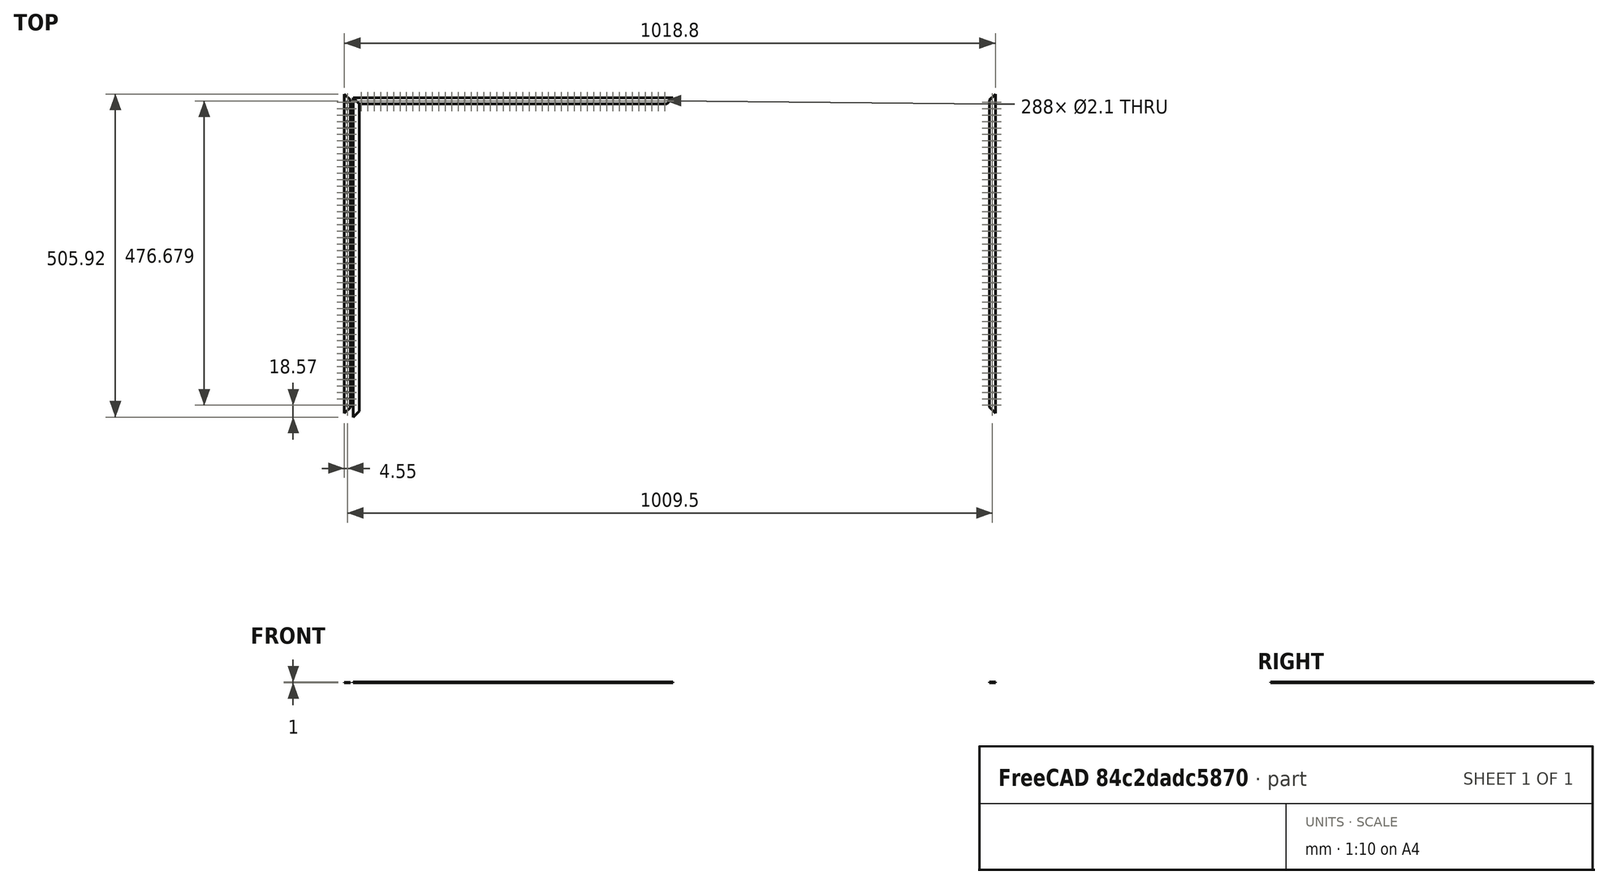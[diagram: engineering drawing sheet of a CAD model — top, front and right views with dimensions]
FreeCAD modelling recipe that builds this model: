
FCSTD DOCUMENT  (FreeCAD 0.21R)
Label: panneaux_solaires
License: All rights reserved
LicenseURL: http://en.wikipedia.org/wiki/All_rights_reserved
objects: Sketcher::SketchObject×112, PartDesign::Body×106, PartDesign::Pad×102, PartDesign::Pocket×8, App::DocumentObjectGroup×2, Part::Feature×1, Fem::ConstraintFixed×1, Fem::ConstraintForce×1, App::MaterialObjectPython×1, Fem::FemAnalysis×1
note: 439 computed .brp shape members not serialized (recipe doc carries the construction recipe); baked Part::Feature solids carry a one-line shape summary decoded from their .brp

FEATURE [Sketcher::SketchObject] Sketch001
  FullyConstrained = true
  MapMode = 5
  Placement = pos=(0,0,0) rot=(1,0,0;1.5708rad)
  sketch-geometry (8):
    g0: LineSegment StartX=0 StartY=0 StartZ=0 EndX=0 EndY=9.5 EndZ=0
    g1: LineSegment StartX=0 StartY=9.5 StartZ=0 EndX=1 EndY=9.5 EndZ=0
    g2: LineSegment StartX=1 StartY=9.5 StartZ=0 EndX=1 EndY=0 EndZ=0
    g3: LineSegment StartX=1 StartY=0 StartZ=0 EndX=0.8 EndY=0 EndZ=0
    g4: LineSegment StartX=0 StartY=0 StartZ=0 EndX=0.2 EndY=0 EndZ=0
    g5: LineSegment StartX=0.2 StartY=0 StartZ=0 EndX=0.2 EndY=9.3 EndZ=0
    g6: LineSegment StartX=0.2 StartY=9.3 StartZ=0 EndX=0.8 EndY=9.3 EndZ=0
    g7: LineSegment StartX=0.8 StartY=9.3 StartZ=0 EndX=0.8 EndY=0 EndZ=0
  constraints (23):
    c: Coincident(g0,g-1)
    c: PointOnObject(g0,g-2)
    c: Coincident(g1,g0)
    c: Horizontal(g1)
    c: Coincident(g2,g1)
    c: Vertical(g2)
    c: Coincident(g3,g2)
    c: Horizontal(g3)
    c: DistanceY(g2,g2) = 9.5
    c: DistanceY(g0,g0) = 9.5
    c: Coincident(g4,g0)
    c: PointOnObject(g4,g-1)
    c: Coincident(g5,g4)
    c: Vertical(g5)
    c: Coincident(g6,g5)
    c: Horizontal(g6)
    c: Coincident(g7,g6)
    c: Coincident(g7,g3)
    c: Vertical(g7)
    c: DistanceX(g1,g1) = 1
    c: DistanceX(g6,g6) = 0.6
    c: DistanceX(g4,g4) = 0.2
    c: DistanceY(g5,g5) = 9.3
FEATURE [PartDesign::Pad] Pad
  Direction = (0,-1,2e-16)
  Length = 500
  Length2 = 10
  Placement = pos=(0,0,0) rot=(1,0,0;1.5708rad)
  Profile = -> Sketch001
  ReferenceAxis = -> Sketch001 [N_Axis]
  Type = 0
FEATURE [Sketcher::SketchObject] Sketch
  FullyConstrained = false
  MapMode = 5
  Placement = pos=(0,0,0) rot=(0.57735,0.57735,0.57735;2.0944rad)
  sketch-geometry (3):
    g0: LineSegment StartX=0 StartY=-2.13969e-08 StartZ=0 EndX=0 EndY=9.5 EndZ=0
    g1: LineSegment StartX=-1.06984e-08 StartY=9.5 StartZ=0 EndX=-9.5 EndY=0 EndZ=0
    g2: LineSegment StartX=-9.5 StartY=0 StartZ=0 EndX=0 EndY=0 EndZ=0
  constraints (5):
    c: Vertical(g0)
    c: Horizontal(g2)
    c: DistanceX(g2,g2) = 9.5
    c: DistanceY(g0,g0) = 9.5
    c: Angle(g2,g1) = 0.785398
FEATURE [PartDesign::Pocket] Pocket
  BaseFeature = -> Pad
  Direction = (-1,-1e-16,1e-16)
  Length = 5
  Length2 = 5
  Placement = pos=(0,0,0) rot=(1,0,0;1.5708rad)
  Profile = -> Sketch
  ReferenceAxis = -> Sketch [N_Axis]
  Reversed = true
  Type = 1
FEATURE [Sketcher::SketchObject] Sketch002
  FullyConstrained = false
  MapMode = 5
  Placement = pos=(0,0,0) rot=(0.57735,0.57735,0.57735;2.0944rad)
  sketch-geometry (3):
    g0: LineSegment StartX=-500 StartY=0 StartZ=0 EndX=-490.5 EndY=0 EndZ=0
    g1: LineSegment StartX=-500 StartY=0 StartZ=0 EndX=-500 EndY=9.5 EndZ=0
    g2: LineSegment StartX=-490.5 StartY=0 StartZ=0 EndX=-500 EndY=9.5 EndZ=0
  constraints (7):
    c: Horizontal(g0)
    c: DistanceX(g0,g0) = 9.5
    c: Coincident(g1,g0)
    c: Vertical(g1)
    c: Coincident(g2,g0)
    c: Coincident(g2,g1)
    c: DistanceY(g1,g1) = 9.5
FEATURE [PartDesign::Pocket] Pocket001  label="cadre découoé"
  BaseFeature = -> Pocket
  Direction = (-1,-1e-16,1e-16)
  Length = 5
  Length2 = 5
  Placement = pos=(0,0,0) rot=(1,0,0;1.5708rad)
  Profile = -> Sketch002
  ReferenceAxis = -> Sketch002 [N_Axis]
  Reversed = true
  Type = 1
FEATURE [PartDesign::Body] Body  label="cadre gauche alu"
  Group = -> [Sketch001,Pad,Sketch,Pocket,Sketch002,Pocket001]
  Origin = -> Origin
  Placement = pos=(14.0463,-5.92123,0) rot=(0,0,0;1.5708rad)
  Tip = -> Pocket001
FEATURE [PartDesign::Body] Body002  label="percage pour rivet 7340a 2/3mm de structure"
  Origin = -> Origin002
FEATURE [Sketcher::SketchObject] Sketch007
  FullyConstrained = false
  MapMode = 5
  Placement = pos=(0,0.3,0) rot=(1,0,0;1.5708rad)
  sketch-geometry (8):
    g0: LineSegment StartX=0.6 StartY=9 StartZ=0 EndX=0.6 EndY=0 EndZ=0
    g1: LineSegment StartX=0.1 StartY=0 StartZ=0 EndX=0.1 EndY=8.9 EndZ=0
    g2: LineSegment StartX=0.1 StartY=8.9 StartZ=0 EndX=0.5 EndY=8.9 EndZ=0
    g3: LineSegment StartX=0.5 StartY=8.9 StartZ=0 EndX=0.5 EndY=0 EndZ=0
    g4: LineSegment StartX=0.6 StartY=0 StartZ=0 EndX=0.5 EndY=0 EndZ=0
    g5: LineSegment StartX=0 StartY=9 StartZ=0 EndX=0.6 EndY=9 EndZ=0
    g6: LineSegment StartX=0.1 StartY=0 StartZ=0 EndX=0 EndY=0 EndZ=0
    g7: LineSegment StartX=0 StartY=0 StartZ=0 EndX=0 EndY=9 EndZ=0
  constraints (21):
    c: Vertical(g0)
    c: DistanceY(g0,g0) = 9
    c: PointOnObject(g1,g-1)
    c: Vertical(g1)
    c: Coincident(g2,g1)
    c: Horizontal(g2)
    c: Coincident(g3,g2)
    c: Vertical(g3)
    c: DistanceX(g2,g2) = 0.4
    c: DistanceX(g-1,g1) = 0.1
    c: DistanceY(g1,g1) = 8.9
    c: Coincident(g4,g0)
    c: Coincident(g4,g3)
    c: Horizontal(g4)
    c: Coincident(g5,g0)
    c: Horizontal(g5)
    c: Coincident(g6,g1)
    c: Coincident(g6,g-1)
    c: Coincident(g7,g6)
    c: Coincident(g7,g5)
    c: Vertical(g7)
FEATURE [PartDesign::Pad] Pad001
  Direction = (0,-1,2e-16)
  Length = 500
  Length2 = 10
  Placement = pos=(0,0.3,0) rot=(1,0,0;1.5708rad)
  Profile = -> Sketch007
  ReferenceAxis = -> Sketch007 [N_Axis]
  Type = 0
FEATURE [Sketcher::SketchObject] Sketch008
  FullyConstrained = false
  MapMode = 5
  Placement = pos=(0,0,0) rot=(0.57735,0.57735,0.57735;2.0944rad)
  sketch-geometry (6):
    g0: LineSegment StartX=-499.7 StartY=9.2 StartZ=0 EndX=-499.7 EndY=-0.3 EndZ=0
    g1: LineSegment StartX=-499.7 StartY=-0.3 StartZ=0 EndX=-490.2 EndY=-0.3 EndZ=0
    g2: LineSegment StartX=-490.2 StartY=-0.3 StartZ=0 EndX=-499.7 EndY=9.2 EndZ=0
    g3: LineSegment StartX=0.3 StartY=-0.3 StartZ=0 EndX=-9.2 EndY=-0.3 EndZ=0
    g4: LineSegment StartX=0.3 StartY=-0.3 StartZ=0 EndX=0.3 EndY=9.2 EndZ=0
    g5: LineSegment StartX=0.3 StartY=9.2 StartZ=0 EndX=-9.2 EndY=-0.3 EndZ=0
  constraints (12):
    c: Vertical(g0)
    c: Horizontal(g1)
    c: Coincident(g2,g1)
    c: Coincident(g2,g0)
    c: DistanceY(g0,g0) = 9.5
    c: DistanceX(g1,g1) = 9.5
    c: Coincident(g4,g3)
    c: Vertical(g4)
    c: Coincident(g5,g3)
    c: Angle(g4,g3) = 1.5708
    c: DistanceY(g4,g4) = 9.5
    c: DistanceX(g3,g3) = 9.5
FEATURE [PartDesign::Pocket] Pocket002
  BaseFeature = -> Pad001
  Direction = (-1,-1e-16,1e-16)
  Length = 5
  Length2 = 5
  Placement = pos=(0,0.3,0) rot=(1,0,0;1.5708rad)
  Profile = -> Sketch008
  ReferenceAxis = -> Sketch008 [N_Axis]
  Reversed = true
  Type = 1
FEATURE [Sketcher::SketchObject] Sketch006
  FullyConstrained = true
  MapMode = 5
  sketch-geometry (48):
    g0: Circle CenterX=-4.75 CenterY=-487.35 CenterZ=0 NormalX=0 NormalY=0 NormalZ=1 AngleXU=0 Radius=1.05
    g1: Circle CenterX=-4.75 CenterY=-477.25 CenterZ=0 NormalX=0 NormalY=0 NormalZ=1 AngleXU=0 Radius=1.05
    g2: Circle CenterX=-4.75 CenterY=-457.05 CenterZ=0 NormalX=0 NormalY=0 NormalZ=1 AngleXU=0 Radius=1.05
    g3: Circle CenterX=-4.75 CenterY=-467.15 CenterZ=0 NormalX=0 NormalY=0 NormalZ=1 AngleXU=0 Radius=1.05
    g4: Circle CenterX=-4.75 CenterY=-416.65 CenterZ=0 NormalX=0 NormalY=0 NormalZ=1 AngleXU=0 Radius=1.05
    g5: Circle CenterX=-4.75 CenterY=-426.75 CenterZ=0 NormalX=0 NormalY=0 NormalZ=1 AngleXU=0 Radius=1.05
    g6: Circle CenterX=-4.75 CenterY=-436.85 CenterZ=0 NormalX=0 NormalY=0 NormalZ=1 AngleXU=0 Radius=1.05
    g7: Circle CenterX=-4.75 CenterY=-446.95 CenterZ=0 NormalX=0 NormalY=0 NormalZ=1 AngleXU=0 Radius=1.05
    g8: Circle CenterX=-4.75 CenterY=-335.85 CenterZ=0 NormalX=0 NormalY=0 NormalZ=1 AngleXU=0 Radius=1.05
    g9: Circle CenterX=-4.75 CenterY=-345.95 CenterZ=0 NormalX=0 NormalY=0 NormalZ=1 AngleXU=0 Radius=1.05
    g10: Circle CenterX=-4.75 CenterY=-356.05 CenterZ=0 NormalX=0 NormalY=0 NormalZ=1 AngleXU=0 Radius=1.05
    g11: Circle CenterX=-4.75 CenterY=-366.15 CenterZ=0 NormalX=0 NormalY=0 NormalZ=1 AngleXU=0 Radius=1.05
    g12: Circle CenterX=-4.75 CenterY=-376.25 CenterZ=0 NormalX=0 NormalY=0 NormalZ=1 AngleXU=0 Radius=1.05
    g13: Circle CenterX=-4.75 CenterY=-386.35 CenterZ=0 NormalX=0 NormalY=0 NormalZ=1 AngleXU=0 Radius=1.05
    g14: Circle CenterX=-4.75 CenterY=-396.45 CenterZ=0 NormalX=0 NormalY=0 NormalZ=1 AngleXU=0 Radius=1.05
    g15: Circle CenterX=-4.75 CenterY=-406.55 CenterZ=0 NormalX=0 NormalY=0 NormalZ=1 AngleXU=0 Radius=1.05
    g16: Circle CenterX=-4.75 CenterY=-174.25 CenterZ=0 NormalX=0 NormalY=0 NormalZ=1 AngleXU=0 Radius=1.05
    g17: Circle CenterX=-4.75 CenterY=-184.35 CenterZ=0 NormalX=0 NormalY=0 NormalZ=1 AngleXU=0 Radius=1.05
    g18: Circle CenterX=-4.75 CenterY=-194.45 CenterZ=0 NormalX=0 NormalY=0 NormalZ=1 AngleXU=0 Radius=1.05
    g19: Circle CenterX=-4.75 CenterY=-204.55 CenterZ=0 NormalX=0 NormalY=0 NormalZ=1 AngleXU=0 Radius=1.05
    g20: Circle CenterX=-4.75 CenterY=-214.65 CenterZ=0 NormalX=0 NormalY=0 NormalZ=1 AngleXU=0 Radius=1.05
    g21: Circle CenterX=-4.75 CenterY=-224.75 CenterZ=0 NormalX=0 NormalY=0 NormalZ=1 AngleXU=0 Radius=1.05
    g22: Circle CenterX=-4.75 CenterY=-234.85 CenterZ=0 NormalX=0 NormalY=0 NormalZ=1 AngleXU=0 Radius=1.05
    g23: Circle CenterX=-4.75 CenterY=-244.95 CenterZ=0 NormalX=0 NormalY=0 NormalZ=1 AngleXU=0 Radius=1.05
    g24: Circle CenterX=-4.75 CenterY=-255.05 CenterZ=0 NormalX=0 NormalY=0 NormalZ=1 AngleXU=0 Radius=1.05
    g25: Circle CenterX=-4.75 CenterY=-265.15 CenterZ=0 NormalX=0 NormalY=0 NormalZ=1 AngleXU=0 Radius=1.05
    g26: Circle CenterX=-4.75 CenterY=-275.25 CenterZ=0 NormalX=0 NormalY=0 NormalZ=1 AngleXU=0 Radius=1.05
    g27: Circle CenterX=-4.75 CenterY=-285.35 CenterZ=0 NormalX=0 NormalY=0 NormalZ=1 AngleXU=0 Radius=1.05
    g28: Circle CenterX=-4.75 CenterY=-295.45 CenterZ=0 NormalX=0 NormalY=0 NormalZ=1 AngleXU=0 Radius=1.05
    g29: Circle CenterX=-4.75 CenterY=-305.55 CenterZ=0 NormalX=0 NormalY=0 NormalZ=1 AngleXU=0 Radius=1.05
    g30: Circle CenterX=-4.75 CenterY=-315.65 CenterZ=0 NormalX=0 NormalY=0 NormalZ=1 AngleXU=0 Radius=1.05
    g31: Circle CenterX=-4.75 CenterY=-325.75 CenterZ=0 NormalX=0 NormalY=0 NormalZ=1 AngleXU=0 Radius=1.05
    g32: Circle CenterX=-4.75 CenterY=-63.15 CenterZ=0 NormalX=0 NormalY=0 NormalZ=1 AngleXU=0 Radius=1.05
    g33: Circle CenterX=-4.75 CenterY=-73.25 CenterZ=0 NormalX=0 NormalY=0 NormalZ=1 AngleXU=0 Radius=1.05
    g34: Circle CenterX=-4.75 CenterY=-83.35 CenterZ=0 NormalX=0 NormalY=0 NormalZ=1 AngleXU=0 Radius=1.05
    g35: Circle CenterX=-4.75 CenterY=-93.45 CenterZ=0 NormalX=0 NormalY=0 NormalZ=1 AngleXU=0 Radius=1.05
    g36: Circle CenterX=-4.75 CenterY=-103.55 CenterZ=0 NormalX=0 NormalY=0 NormalZ=1 AngleXU=0 Radius=1.05
    g37: Circle CenterX=-4.75 CenterY=-113.65 CenterZ=0 NormalX=0 NormalY=0 NormalZ=1 AngleXU=0 Radius=1.05
    g38: Circle CenterX=-4.75 CenterY=-123.75 CenterZ=0 NormalX=0 NormalY=0 NormalZ=1 AngleXU=0 Radius=1.05
    g39: Circle CenterX=-4.75 CenterY=-133.85 CenterZ=0 NormalX=0 NormalY=0 NormalZ=1 AngleXU=0 Radius=1.05
    g40: Circle CenterX=-4.75 CenterY=-143.95 CenterZ=0 NormalX=0 NormalY=0 NormalZ=1 AngleXU=0 Radius=1.05
    g41: Circle CenterX=-4.75 CenterY=-154.05 CenterZ=0 NormalX=0 NormalY=0 NormalZ=1 AngleXU=0 Radius=1.05
    g42: Circle CenterX=-4.75 CenterY=-164.15 CenterZ=0 NormalX=0 NormalY=0 NormalZ=1 AngleXU=0 Radius=1.05
    g43: Circle CenterX=-4.75 CenterY=-12.65 CenterZ=0 NormalX=0 NormalY=0 NormalZ=1 AngleXU=0 Radius=1.05
    g44: Circle CenterX=-4.75 CenterY=-22.75 CenterZ=0 NormalX=0 NormalY=0 NormalZ=1 AngleXU=0 Radius=1.05
    g45: Circle CenterX=-4.75 CenterY=-32.85 CenterZ=0 NormalX=0 NormalY=0 NormalZ=1 AngleXU=0 Radius=1.05
    g46: Circle CenterX=-4.75 CenterY=-42.95 CenterZ=0 NormalX=0 NormalY=0 NormalZ=1 AngleXU=0 Radius=1.05
    g47: Circle CenterX=-4.75 CenterY=-53.05 CenterZ=0 NormalX=0 NormalY=0 NormalZ=1 AngleXU=0 Radius=1.05
  constraints (144):
    c: Diameter(g0) = 2.1
    c: Equal(g0,g1) = 2.1
    c: DistanceY(g0,g1) = 10.1
    c: Equal(g0,g3) = 2.1
    c: Equal(g3,g2) = 2.1
    c: DistanceY(g3,g2) = 10.1
    c: Equal(g0,g7) = 2.1
    c: Equal(g7,g6) = 2.1
    c: DistanceY(g7,g6) = 10.1
    c: Equal(g7,g5) = 2.1
    c: Equal(g5,g4) = 2.1
    c: DistanceY(g5,g4) = 10.1
    c: Equal(g0,g15) = 2.1
    c: Equal(g15,g14) = 2.1
    c: DistanceY(g15,g14) = 10.1
    c: Equal(g15,g13) = 2.1
    c: Equal(g13,g12) = 2.1
    c: DistanceY(g13,g12) = 10.1
    c: Equal(g15,g11) = 2.1
    c: Equal(g11,g10) = 2.1
    c: DistanceY(g11,g10) = 10.1
    c: Equal(g11,g9) = 2.1
    c: Equal(g9,g8) = 2.1
    c: DistanceY(g9,g8) = 10.1
    c: Equal(g0,g31) = 2.1
    c: Equal(g31,g30) = 2.1
    c: DistanceY(g31,g30) = 10.1
    c: Equal(g31,g29) = 2.1
    c: Equal(g29,g28) = 2.1
    c: DistanceY(g29,g28) = 10.1
    c: Equal(g31,g27) = 2.1
    c: Equal(g27,g26) = 2.1
    c: DistanceY(g27,g26) = 10.1
    c: Equal(g27,g25) = 2.1
    c: Equal(g25,g24) = 2.1
    c: DistanceY(g25,g24) = 10.1
    c: Equal(g31,g23) = 2.1
    c: Equal(g23,g22) = 2.1
    c: DistanceY(g23,g22) = 10.1
    c: Equal(g23,g21) = 2.1
    c: Equal(g21,g20) = 2.1
    c: DistanceY(g21,g20) = 10.1
    c: Equal(g23,g19) = 2.1
    c: Equal(g19,g18) = 2.1
    c: DistanceY(g19,g18) = 10.1
    c: Equal(g19,g17) = 2.1
    c: Equal(g17,g16) = 2.1
    c: DistanceY(g17,g16) = 10.1
    c: Equal(g42,g41) = 2.1
    c: DistanceY(g42,g41) = 10.1
    c: Equal(g42,g40) = 2.1
    c: Equal(g40,g39) = 2.1
    c: DistanceY(g40,g39) = 10.1
    c: Equal(g38,g37) = 2.1
    c: DistanceY(g38,g37) = 10.1
    c: Equal(g38,g36) = 2.1
    c: Equal(g36,g35) = 2.1
    c: DistanceY(g36,g35) = 10.1
    c: Equal(g38,g34) = 2.1
    c: Equal(g34,g33) = 2.1
    c: DistanceY(g34,g33) = 10.1
    c: Equal(g34,g32) = 2.1
    c: Equal(g47,g46) = 2.1
    c: DistanceY(g47,g46) = 10.1
    c: Equal(g45,g44) = 2.1
    c: DistanceY(g45,g44) = 10.1
    c: Equal(g45,g43) = 2.1
    c: DistanceY(g1,g3) = 10.1
    c: DistanceY(g2,g7) = 10.1
    c: DistanceY(g6,g5) = 10.1
    c: DistanceY(g4,g15) = 10.1
    c: DistanceY(g14,g13) = 10.1
    c: DistanceY(g8,g31) = 10.1
    c: DistanceY(g30,g29) = 10.1
    c: DistanceY(g28,g27) = 10.1
    c: DistanceY(g26,g25) = 10.1
    c: DistanceY(g24,g23) = 10.1
    c: DistanceY(g22,g21) = 10.1
    c: DistanceY(g20,g19) = 10.1
    c: DistanceY(g18,g17) = 10.1
    c: DistanceY(g16,g42) = 10.1
    c: DistanceY(g39,g38) = 10.1
    c: DistanceY(g37,g36) = 10.1
    c: DistanceY(g35,g34) = 10.1
    c: DistanceY(g33,g32) = 10.1
    c: DistanceY(g46,g45) = 10.1
    c: DistanceY(g32,g47) = 10.1
    c: DistanceY(g44,g43) = 10.1
    c: DistanceY(g12,g11) = 10.1
    c: DistanceY(g10,g9) = 10.1
    c: DistanceY(g41,g40) = 10.1
    c: DistanceY(g43,g-1) = 12.65
    c: DistanceX(g43,g-1) = 4.75
    c: DistanceX(g44,g-1) = 4.75
    c: DistanceX(g45,g-1) = 4.75
    c: DistanceX(g47,g-1) = 4.75
    c: DistanceX(g32,g-1) = 4.75
    c: DistanceX(g34,g-1) = 4.75
    c: DistanceX(g35,g-1) = 4.75
    c: DistanceX(g0,g-1) = 4.75
    c: DistanceX(g1,g-1) = 4.75
    c: DistanceX(g3,g-1) = 4.75
    c: DistanceX(g2,g-1) = 4.75
    c: DistanceX(g7,g-1) = 4.75
    c: DistanceX(g6,g-1) = 4.75
    c: DistanceX(g5,g-1) = 4.75
    c: DistanceX(g4,g-1) = 4.75
    c: DistanceX(g15,g-1) = 4.75
    c: DistanceX(g14,g-1) = 4.75
    c: DistanceX(g13,g-1) = 4.75
    c: DistanceX(g12,g-1) = 4.75
    c: DistanceX(g11,g-1) = 4.75
    c: DistanceX(g10,g-1) = 4.75
    c: DistanceX(g9,g-1) = 4.75
    c: DistanceX(g8,g-1) = 4.75
    c: DistanceX(g31,g-1) = 4.75
    c: DistanceX(g30,g-1) = 4.75
    c: DistanceX(g29,g-1) = 4.75
    c: DistanceX(g28,g-1) = 4.75
    c: DistanceX(g27,g-1) = 4.75
    c: DistanceX(g26,g-1) = 4.75
    c: DistanceX(g25,g-1) = 4.75
    c: DistanceX(g24,g-1) = 4.75
    c: DistanceX(g23,g-1) = 4.75
    c: DistanceX(g22,g-1) = 4.75
    c: DistanceX(g21,g-1) = 4.75
    c: DistanceX(g20,g-1) = 4.75
    c: DistanceX(g19,g-1) = 4.75
    c: DistanceX(g18,g-1) = 4.75
    c: DistanceX(g17,g-1) = 4.75
    c: DistanceX(g16,g-1) = 4.75
    c: DistanceX(g42,g-1) = 4.75
    c: DistanceX(g41,g-1) = 4.75
    c: DistanceX(g40,g-1) = 4.75
    c: DistanceX(g39,g-1) = 4.75
    c: DistanceX(g38,g-1) = 4.75
    c: DistanceX(g37,g-1) = 4.75
    c: DistanceX(g36,g-1) = 4.75
    c: DistanceX(g33,g-1) = 4.75
    c: DistanceX(g46,g-1) = 4.75
    c: Diameter(g43) = 2.1
    c: Diameter(g46) = 2.1
    c: Diameter(g32) = 2.1
    c: Diameter(g39) = 2.1
FEATURE [PartDesign::Body] Body003  label="Corps"
  Group = -> [Sketch006]
  Origin = -> Origin003
FEATURE [Sketcher::SketchObject] Sketch010
  FullyConstrained = true
  MapMode = 5
  Placement = pos=(0,0.3,-0.3) rot=(0,1,0;1.5708rad)
  sketch-geometry (48):
    g0: Circle CenterX=-4.75 CenterY=-487.35 CenterZ=0 NormalX=0 NormalY=0 NormalZ=1 AngleXU=0 Radius=1.05
    g1: Circle CenterX=-4.75 CenterY=-477.25 CenterZ=0 NormalX=0 NormalY=0 NormalZ=1 AngleXU=0 Radius=1.05
    g2: Circle CenterX=-4.75 CenterY=-457.05 CenterZ=0 NormalX=0 NormalY=0 NormalZ=1 AngleXU=0 Radius=1.05
    g3: Circle CenterX=-4.75 CenterY=-467.15 CenterZ=0 NormalX=0 NormalY=0 NormalZ=1 AngleXU=0 Radius=1.05
    g4: Circle CenterX=-4.75 CenterY=-416.65 CenterZ=0 NormalX=0 NormalY=0 NormalZ=1 AngleXU=0 Radius=1.05
    g5: Circle CenterX=-4.75 CenterY=-426.75 CenterZ=0 NormalX=0 NormalY=0 NormalZ=1 AngleXU=0 Radius=1.05
    g6: Circle CenterX=-4.75 CenterY=-436.85 CenterZ=0 NormalX=0 NormalY=0 NormalZ=1 AngleXU=0 Radius=1.05
    g7: Circle CenterX=-4.75 CenterY=-446.95 CenterZ=0 NormalX=0 NormalY=0 NormalZ=1 AngleXU=0 Radius=1.05
    g8: Circle CenterX=-4.75 CenterY=-335.85 CenterZ=0 NormalX=0 NormalY=0 NormalZ=1 AngleXU=0 Radius=1.05
    g9: Circle CenterX=-4.75 CenterY=-345.95 CenterZ=0 NormalX=0 NormalY=0 NormalZ=1 AngleXU=0 Radius=1.05
    g10: Circle CenterX=-4.75 CenterY=-356.05 CenterZ=0 NormalX=0 NormalY=0 NormalZ=1 AngleXU=0 Radius=1.05
    g11: Circle CenterX=-4.75 CenterY=-366.15 CenterZ=0 NormalX=0 NormalY=0 NormalZ=1 AngleXU=0 Radius=1.05
    g12: Circle CenterX=-4.75 CenterY=-376.25 CenterZ=0 NormalX=0 NormalY=0 NormalZ=1 AngleXU=0 Radius=1.05
    g13: Circle CenterX=-4.75 CenterY=-386.35 CenterZ=0 NormalX=0 NormalY=0 NormalZ=1 AngleXU=0 Radius=1.05
    g14: Circle CenterX=-4.75 CenterY=-396.45 CenterZ=0 NormalX=0 NormalY=0 NormalZ=1 AngleXU=0 Radius=1.05
    g15: Circle CenterX=-4.75 CenterY=-406.55 CenterZ=0 NormalX=0 NormalY=0 NormalZ=1 AngleXU=0 Radius=1.05
    g16: Circle CenterX=-4.75 CenterY=-174.25 CenterZ=0 NormalX=0 NormalY=0 NormalZ=1 AngleXU=0 Radius=1.05
    g17: Circle CenterX=-4.75 CenterY=-184.35 CenterZ=0 NormalX=0 NormalY=0 NormalZ=1 AngleXU=0 Radius=1.05
    g18: Circle CenterX=-4.75 CenterY=-194.45 CenterZ=0 NormalX=0 NormalY=0 NormalZ=1 AngleXU=0 Radius=1.05
    g19: Circle CenterX=-4.75 CenterY=-204.55 CenterZ=0 NormalX=0 NormalY=0 NormalZ=1 AngleXU=0 Radius=1.05
    g20: Circle CenterX=-4.75 CenterY=-214.65 CenterZ=0 NormalX=0 NormalY=0 NormalZ=1 AngleXU=0 Radius=1.05
    g21: Circle CenterX=-4.75 CenterY=-224.75 CenterZ=0 NormalX=0 NormalY=0 NormalZ=1 AngleXU=0 Radius=1.05
    g22: Circle CenterX=-4.75 CenterY=-234.85 CenterZ=0 NormalX=0 NormalY=0 NormalZ=1 AngleXU=0 Radius=1.05
    g23: Circle CenterX=-4.75 CenterY=-244.95 CenterZ=0 NormalX=0 NormalY=0 NormalZ=1 AngleXU=0 Radius=1.05
    g24: Circle CenterX=-4.75 CenterY=-255.05 CenterZ=0 NormalX=0 NormalY=0 NormalZ=1 AngleXU=0 Radius=1.05
    g25: Circle CenterX=-4.75 CenterY=-265.15 CenterZ=0 NormalX=0 NormalY=0 NormalZ=1 AngleXU=0 Radius=1.05
    g26: Circle CenterX=-4.75 CenterY=-275.25 CenterZ=0 NormalX=0 NormalY=0 NormalZ=1 AngleXU=0 Radius=1.05
    g27: Circle CenterX=-4.75 CenterY=-285.35 CenterZ=0 NormalX=0 NormalY=0 NormalZ=1 AngleXU=0 Radius=1.05
    g28: Circle CenterX=-4.75 CenterY=-295.45 CenterZ=0 NormalX=0 NormalY=0 NormalZ=1 AngleXU=0 Radius=1.05
    g29: Circle CenterX=-4.75 CenterY=-305.55 CenterZ=0 NormalX=0 NormalY=0 NormalZ=1 AngleXU=0 Radius=1.05
    g30: Circle CenterX=-4.75 CenterY=-315.65 CenterZ=0 NormalX=0 NormalY=0 NormalZ=1 AngleXU=0 Radius=1.05
    g31: Circle CenterX=-4.75 CenterY=-325.75 CenterZ=0 NormalX=0 NormalY=0 NormalZ=1 AngleXU=0 Radius=1.05
    g32: Circle CenterX=-4.75 CenterY=-63.15 CenterZ=0 NormalX=0 NormalY=0 NormalZ=1 AngleXU=0 Radius=1.05
    g33: Circle CenterX=-4.75 CenterY=-73.25 CenterZ=0 NormalX=0 NormalY=0 NormalZ=1 AngleXU=0 Radius=1.05
    g34: Circle CenterX=-4.75 CenterY=-83.35 CenterZ=0 NormalX=0 NormalY=0 NormalZ=1 AngleXU=0 Radius=1.05
    g35: Circle CenterX=-4.75 CenterY=-93.45 CenterZ=0 NormalX=0 NormalY=0 NormalZ=1 AngleXU=0 Radius=1.05
    g36: Circle CenterX=-4.75 CenterY=-103.55 CenterZ=0 NormalX=0 NormalY=0 NormalZ=1 AngleXU=0 Radius=1.05
    g37: Circle CenterX=-4.75 CenterY=-113.65 CenterZ=0 NormalX=0 NormalY=0 NormalZ=1 AngleXU=0 Radius=1.05
    g38: Circle CenterX=-4.75 CenterY=-123.75 CenterZ=0 NormalX=0 NormalY=0 NormalZ=1 AngleXU=0 Radius=1.05
    g39: Circle CenterX=-4.75 CenterY=-133.85 CenterZ=0 NormalX=0 NormalY=0 NormalZ=1 AngleXU=0 Radius=1.05
    g40: Circle CenterX=-4.75 CenterY=-143.95 CenterZ=0 NormalX=0 NormalY=0 NormalZ=1 AngleXU=0 Radius=1.05
    g41: Circle CenterX=-4.75 CenterY=-154.05 CenterZ=0 NormalX=0 NormalY=0 NormalZ=1 AngleXU=0 Radius=1.05
    g42: Circle CenterX=-4.75 CenterY=-164.15 CenterZ=0 NormalX=0 NormalY=0 NormalZ=1 AngleXU=0 Radius=1.05
    g43: Circle CenterX=-4.75 CenterY=-12.65 CenterZ=0 NormalX=0 NormalY=0 NormalZ=1 AngleXU=0 Radius=1.05
    g44: Circle CenterX=-4.75 CenterY=-22.75 CenterZ=0 NormalX=0 NormalY=0 NormalZ=1 AngleXU=0 Radius=1.05
    g45: Circle CenterX=-4.75 CenterY=-32.85 CenterZ=0 NormalX=0 NormalY=0 NormalZ=1 AngleXU=0 Radius=1.05
    g46: Circle CenterX=-4.75 CenterY=-42.95 CenterZ=0 NormalX=0 NormalY=0 NormalZ=1 AngleXU=0 Radius=1.05
    g47: Circle CenterX=-4.75 CenterY=-53.05 CenterZ=0 NormalX=0 NormalY=0 NormalZ=1 AngleXU=0 Radius=1.05
  constraints (144):
    c: Diameter(g0) = 2.1
    c: Equal(g0,g1) = 2.1
    c: DistanceY(g0,g1) = 10.1
    c: Equal(g0,g3) = 2.1
    c: Equal(g3,g2) = 2.1
    c: DistanceY(g3,g2) = 10.1
    c: Equal(g0,g7) = 2.1
    c: Equal(g7,g6) = 2.1
    c: DistanceY(g7,g6) = 10.1
    c: Equal(g7,g5) = 2.1
    c: Equal(g5,g4) = 2.1
    c: DistanceY(g5,g4) = 10.1
    c: Equal(g0,g15) = 2.1
    c: Equal(g15,g14) = 2.1
    c: DistanceY(g15,g14) = 10.1
    c: Equal(g15,g13) = 2.1
    c: Equal(g13,g12) = 2.1
    c: DistanceY(g13,g12) = 10.1
    c: Equal(g15,g11) = 2.1
    c: Equal(g11,g10) = 2.1
    c: DistanceY(g11,g10) = 10.1
    c: Equal(g11,g9) = 2.1
    c: Equal(g9,g8) = 2.1
    c: DistanceY(g9,g8) = 10.1
    c: Equal(g0,g31) = 2.1
    c: Equal(g31,g30) = 2.1
    c: DistanceY(g31,g30) = 10.1
    c: Equal(g31,g29) = 2.1
    c: Equal(g29,g28) = 2.1
    c: DistanceY(g29,g28) = 10.1
    c: Equal(g31,g27) = 2.1
    c: Equal(g27,g26) = 2.1
    c: DistanceY(g27,g26) = 10.1
    c: Equal(g27,g25) = 2.1
    c: Equal(g25,g24) = 2.1
    c: DistanceY(g25,g24) = 10.1
    c: Equal(g31,g23) = 2.1
    c: Equal(g23,g22) = 2.1
    c: DistanceY(g23,g22) = 10.1
    c: Equal(g23,g21) = 2.1
    c: Equal(g21,g20) = 2.1
    c: DistanceY(g21,g20) = 10.1
    c: Equal(g23,g19) = 2.1
    c: Equal(g19,g18) = 2.1
    c: DistanceY(g19,g18) = 10.1
    c: Equal(g19,g17) = 2.1
    c: Equal(g17,g16) = 2.1
    c: DistanceY(g17,g16) = 10.1
    c: Equal(g42,g41) = 2.1
    c: DistanceY(g42,g41) = 10.1
    c: Equal(g42,g40) = 2.1
    c: Equal(g40,g39) = 2.1
    c: DistanceY(g40,g39) = 10.1
    c: Equal(g38,g37) = 2.1
    c: DistanceY(g38,g37) = 10.1
    c: Equal(g38,g36) = 2.1
    c: Equal(g36,g35) = 2.1
    c: DistanceY(g36,g35) = 10.1
    c: Equal(g38,g34) = 2.1
    c: Equal(g34,g33) = 2.1
    c: DistanceY(g34,g33) = 10.1
    c: Equal(g34,g32) = 2.1
    c: Equal(g47,g46) = 2.1
    c: DistanceY(g47,g46) = 10.1
    c: Equal(g45,g44) = 2.1
    c: DistanceY(g45,g44) = 10.1
    c: Equal(g45,g43) = 2.1
    c: DistanceY(g1,g3) = 10.1
    c: DistanceY(g2,g7) = 10.1
    c: DistanceY(g6,g5) = 10.1
    c: DistanceY(g4,g15) = 10.1
    c: DistanceY(g14,g13) = 10.1
    c: DistanceY(g8,g31) = 10.1
    c: DistanceY(g30,g29) = 10.1
    c: DistanceY(g28,g27) = 10.1
    c: DistanceY(g26,g25) = 10.1
    c: DistanceY(g24,g23) = 10.1
    c: DistanceY(g22,g21) = 10.1
    c: DistanceY(g20,g19) = 10.1
    c: DistanceY(g18,g17) = 10.1
    c: DistanceY(g16,g42) = 10.1
    c: DistanceY(g39,g38) = 10.1
    c: DistanceY(g37,g36) = 10.1
    c: DistanceY(g35,g34) = 10.1
    c: DistanceY(g33,g32) = 10.1
    c: DistanceY(g46,g45) = 10.1
    c: DistanceY(g32,g47) = 10.1
    c: DistanceY(g44,g43) = 10.1
    c: DistanceY(g12,g11) = 10.1
    c: DistanceY(g10,g9) = 10.1
    c: DistanceY(g41,g40) = 10.1
    c: DistanceY(g43,g-1) = 12.65
    c: DistanceX(g43,g-1) = 4.75
    c: DistanceX(g44,g-1) = 4.75
    c: DistanceX(g45,g-1) = 4.75
    c: DistanceX(g47,g-1) = 4.75
    c: DistanceX(g32,g-1) = 4.75
    c: DistanceX(g34,g-1) = 4.75
    c: DistanceX(g35,g-1) = 4.75
    c: DistanceX(g0,g-1) = 4.75
    c: DistanceX(g1,g-1) = 4.75
    c: DistanceX(g3,g-1) = 4.75
    c: DistanceX(g2,g-1) = 4.75
    c: DistanceX(g7,g-1) = 4.75
    c: DistanceX(g6,g-1) = 4.75
    c: DistanceX(g5,g-1) = 4.75
    c: DistanceX(g4,g-1) = 4.75
    c: DistanceX(g15,g-1) = 4.75
    c: DistanceX(g14,g-1) = 4.75
    c: DistanceX(g13,g-1) = 4.75
    c: DistanceX(g12,g-1) = 4.75
    c: DistanceX(g11,g-1) = 4.75
    c: DistanceX(g10,g-1) = 4.75
    c: DistanceX(g9,g-1) = 4.75
    c: DistanceX(g8,g-1) = 4.75
    c: DistanceX(g31,g-1) = 4.75
    c: DistanceX(g30,g-1) = 4.75
    c: DistanceX(g29,g-1) = 4.75
    c: DistanceX(g28,g-1) = 4.75
    c: DistanceX(g27,g-1) = 4.75
    c: DistanceX(g26,g-1) = 4.75
    c: DistanceX(g25,g-1) = 4.75
    c: DistanceX(g24,g-1) = 4.75
    c: DistanceX(g23,g-1) = 4.75
    c: DistanceX(g22,g-1) = 4.75
    c: DistanceX(g21,g-1) = 4.75
    c: DistanceX(g20,g-1) = 4.75
    c: DistanceX(g19,g-1) = 4.75
    c: DistanceX(g18,g-1) = 4.75
    c: DistanceX(g17,g-1) = 4.75
    c: DistanceX(g16,g-1) = 4.75
    c: DistanceX(g42,g-1) = 4.75
    c: DistanceX(g41,g-1) = 4.75
    c: DistanceX(g40,g-1) = 4.75
    c: DistanceX(g39,g-1) = 4.75
    c: DistanceX(g38,g-1) = 4.75
    c: DistanceX(g37,g-1) = 4.75
    c: DistanceX(g36,g-1) = 4.75
    c: DistanceX(g33,g-1) = 4.75
    c: DistanceX(g46,g-1) = 4.75
    c: Diameter(g43) = 2.1
    c: Diameter(g46) = 2.1
    c: Diameter(g32) = 2.1
    c: Diameter(g39) = 2.1
FEATURE [PartDesign::Pocket] Pocket003
  BaseFeature = -> Pocket002
  Direction = (-1,0,-2e-16)
  Length = 10
  Length2 = 5
  Placement = pos=(0,0.3,0) rot=(1,0,0;1.5708rad)
  Profile = -> Sketch010
  ReferenceAxis = -> Sketch010 [N_Axis]
  Refine = true
  Reversed = true
  Type = 1
FEATURE [PartDesign::Body] Body001  label="join caoutchou"
  Group = -> [Sketch007,Pad001,Sketch008,Pocket002,Sketch010,Pocket003]
  Origin = -> Origin001
  Placement = pos=(-0.3,-0.3,0.2) rot=(0,-1,0;1.5708rad)
  Tip = -> Pocket003
FEATURE [Sketcher::SketchObject] Sketch011
  FullyConstrained = true
  MapMode = 5
  sketch-geometry (1):
    g0: Circle CenterX=-4.75 CenterY=-22.75 CenterZ=0 NormalX=0 NormalY=0 NormalZ=1 AngleXU=0 Radius=1.05
  constraints (3):
    c: Diameter(g0) = 2.1
    c: Distance(g0,g-2) = 4.75
    c: Distance(g0,g-1) = 22.75
FEATURE [PartDesign::Pad] Pad003
  Direction = (0,0,1)
  Length = 0.6
  Length2 = 10
  Profile = -> Sketch011
  ReferenceAxis = -> Sketch011 [N_Axis]
  Refine = true
  Type = 0
FEATURE [PartDesign::Body] Body004  label="entretoises"
  Group = -> [Sketch011,Pad003]
  Origin = -> Origin004
  Tip = -> Pad003
FEATURE [Sketcher::SketchObject] Sketch012
  FullyConstrained = true
  MapMode = 5
  Placement = pos=(0,0,0.2) rot=(0,0,1;0rad)
  sketch-geometry (1):
    g0: Circle CenterX=-4.75 CenterY=-12.65 CenterZ=0 NormalX=0 NormalY=0 NormalZ=1 AngleXU=0 Radius=1.05
  constraints (3):
    c: Diameter(g0) = 2.1
    c: Distance(g0,g-2) = 4.75
    c: Distance(g0,g-1) = 12.65
FEATURE [PartDesign::Pad] Pad004
  Direction = (0,0,1)
  Length = 0.6
  Length2 = 10
  Placement = pos=(0,0,0.2) rot=(0,0,1;0rad)
  Profile = -> Sketch012
  ReferenceAxis = -> Sketch012 [N_Axis]
  Refine = true
  Type = 0
FEATURE [PartDesign::Body] Body005  label="entretoises001"
  Group = -> [Sketch012,Pad004]
  Origin = -> Origin005
  Tip = -> Pad004
FEATURE [Sketcher::SketchObject] Sketch013
  FullyConstrained = true
  MapMode = 5
  Placement = pos=(0,0,0.2) rot=(0,0,1;0rad)
  sketch-geometry (1):
    g0: Circle CenterX=-4.75 CenterY=-32.85 CenterZ=0 NormalX=0 NormalY=0 NormalZ=1 AngleXU=0 Radius=1.05
  constraints (3):
    c: Diameter(g0) = 2.1
    c: Distance(g0,g-2) = 4.75
    c: Distance(g0,g-1) = 32.85
FEATURE [PartDesign::Pad] Pad005
  Direction = (0,0,1)
  Length = 0.6
  Length2 = 10
  Placement = pos=(0,0,0.2) rot=(0,0,1;0rad)
  Profile = -> Sketch013
  ReferenceAxis = -> Sketch013 [N_Axis]
  Refine = true
  Type = 0
FEATURE [PartDesign::Body] Body006  label="entretoises002"
  Group = -> [Sketch013,Pad005]
  Origin = -> Origin006
  Tip = -> Pad005
FEATURE [Sketcher::SketchObject] Sketch014
  FullyConstrained = true
  MapMode = 5
  Placement = pos=(0,0,0.2) rot=(0,0,1;0rad)
  sketch-geometry (1):
    g0: Circle CenterX=-4.75 CenterY=-42.95 CenterZ=0 NormalX=0 NormalY=0 NormalZ=1 AngleXU=0 Radius=1.05
  constraints (3):
    c: Diameter(g0) = 2.1
    c: Distance(g0,g-2) = 4.75
    c: Distance(g0,g-1) = 42.95
FEATURE [PartDesign::Pad] Pad006
  Direction = (0,0,1)
  Length = 0.6
  Length2 = 10
  Placement = pos=(0,0,0.2) rot=(0,0,1;0rad)
  Profile = -> Sketch014
  ReferenceAxis = -> Sketch014 [N_Axis]
  Refine = true
  Type = 0
FEATURE [PartDesign::Body] Body007  label="entretoises003"
  Group = -> [Sketch014,Pad006]
  Origin = -> Origin007
  Tip = -> Pad006
FEATURE [Sketcher::SketchObject] Sketch015
  FullyConstrained = true
  MapMode = 5
  Placement = pos=(0,0,0.2) rot=(0,0,1;0rad)
  sketch-geometry (1):
    g0: Circle CenterX=-4.75 CenterY=-53.05 CenterZ=0 NormalX=0 NormalY=0 NormalZ=1 AngleXU=0 Radius=1.05
  constraints (3):
    c: Diameter(g0) = 2.1
    c: Distance(g0,g-2) = 4.75
    c: Distance(g0,g-1) = 53.05
FEATURE [PartDesign::Pad] Pad007
  Direction = (0,0,1)
  Length = 0.6
  Length2 = 10
  Placement = pos=(0,0,0.2) rot=(0,0,1;0rad)
  Profile = -> Sketch015
  ReferenceAxis = -> Sketch015 [N_Axis]
  Refine = true
  Type = 0
FEATURE [PartDesign::Body] Body008  label="entretoises004"
  Group = -> [Sketch015,Pad007]
  Origin = -> Origin008
  Tip = -> Pad007
FEATURE [Sketcher::SketchObject] Sketch016
  FullyConstrained = true
  MapMode = 5
  Placement = pos=(0,0,0.2) rot=(0,0,1;0rad)
  sketch-geometry (1):
    g0: Circle CenterX=-4.75 CenterY=-22.75 CenterZ=0 NormalX=0 NormalY=0 NormalZ=1 AngleXU=0 Radius=1.05
  constraints (3):
    c: Diameter(g0) = 2.1
    c: Distance(g0,g-2) = 4.75
    c: Distance(g0,g-1) = 22.75
FEATURE [PartDesign::Pad] Pad008
  Direction = (0,0,1)
  Length = 0.6
  Length2 = 10
  Placement = pos=(0,0,0.2) rot=(0,0,1;0rad)
  Profile = -> Sketch016
  ReferenceAxis = -> Sketch016 [N_Axis]
  Refine = true
  Type = 0
FEATURE [PartDesign::Body] Body009  label="entretoises005"
  Group = -> [Sketch016,Pad008]
  Origin = -> Origin009
  Tip = -> Pad008
FEATURE [Sketcher::SketchObject] Sketch017
  FullyConstrained = true
  MapMode = 5
  Placement = pos=(0,0,0.2) rot=(0,0,1;0rad)
  sketch-geometry (1):
    g0: Circle CenterX=-4.75 CenterY=-63.15 CenterZ=0 NormalX=0 NormalY=0 NormalZ=1 AngleXU=0 Radius=1.05
  constraints (3):
    c: Diameter(g0) = 2.1
    c: Distance(g0,g-2) = 4.75
    c: Distance(g0,g-1) = 63.15
FEATURE [Sketcher::SketchObject] Sketch018
  FullyConstrained = true
  MapMode = 5
  Placement = pos=(0,0,0.2) rot=(0,0,1;0rad)
  sketch-geometry (1):
    g0: Circle CenterX=-4.75 CenterY=-73.25 CenterZ=0 NormalX=0 NormalY=0 NormalZ=1 AngleXU=0 Radius=1.05
  constraints (3):
    c: Diameter(g0) = 2.1
    c: Distance(g0,g-2) = 4.75
    c: Distance(g0,g-1) = 73.25
FEATURE [PartDesign::Pad] Pad010
  Direction = (0,0,1)
  Length = 0.6
  Length2 = 10
  Placement = pos=(0,0,0.2) rot=(0,0,1;0rad)
  Profile = -> Sketch018
  ReferenceAxis = -> Sketch018 [N_Axis]
  Refine = true
  Type = 0
FEATURE [PartDesign::Body] Body011  label="entretoises007"
  Group = -> [Sketch018,Pad010]
  Origin = -> Origin011
  Tip = -> Pad010
FEATURE [Sketcher::SketchObject] Sketch019
  FullyConstrained = true
  MapMode = 5
  Placement = pos=(0,0,0.2) rot=(0,0,1;0rad)
  sketch-geometry (1):
    g0: Circle CenterX=-4.75 CenterY=-83.35 CenterZ=0 NormalX=0 NormalY=0 NormalZ=1 AngleXU=0 Radius=1.05
  constraints (3):
    c: Diameter(g0) = 2.1
    c: Distance(g0,g-2) = 4.75
    c: Distance(g0,g-1) = 83.35
FEATURE [PartDesign::Pad] Pad011
  Direction = (0,0,1)
  Length = 0.6
  Length2 = 10
  Placement = pos=(0,0,0.2) rot=(0,0,1;0rad)
  Profile = -> Sketch019
  ReferenceAxis = -> Sketch019 [N_Axis]
  Refine = true
  Type = 0
FEATURE [PartDesign::Body] Body012  label="entretoises008"
  Group = -> [Sketch019,Pad011]
  Origin = -> Origin012
  Tip = -> Pad011
FEATURE [Sketcher::SketchObject] Sketch020
  FullyConstrained = true
  MapMode = 5
  Placement = pos=(0,0,0.2) rot=(0,0,1;0rad)
  sketch-geometry (1):
    g0: Circle CenterX=-4.75 CenterY=-93.45 CenterZ=0 NormalX=0 NormalY=0 NormalZ=1 AngleXU=0 Radius=1.05
  constraints (3):
    c: Diameter(g0) = 2.1
    c: Distance(g0,g-2) = 4.75
    c: Distance(g0,g-1) = 93.45
FEATURE [PartDesign::Pad] Pad012
  Direction = (0,0,1)
  Length = 0.6
  Length2 = 10
  Placement = pos=(0,0,0.2) rot=(0,0,1;0rad)
  Profile = -> Sketch020
  ReferenceAxis = -> Sketch020 [N_Axis]
  Refine = true
  Type = 0
FEATURE [PartDesign::Body] Body013  label="entretoises009"
  Group = -> [Sketch020,Pad012]
  Origin = -> Origin013
  Tip = -> Pad012
FEATURE [Sketcher::SketchObject] Sketch021
  FullyConstrained = true
  MapMode = 5
  Placement = pos=(0,0,0.2) rot=(0,0,1;0rad)
  sketch-geometry (1):
    g0: Circle CenterX=-4.75 CenterY=-103.55 CenterZ=0 NormalX=0 NormalY=0 NormalZ=1 AngleXU=0 Radius=1.05
  constraints (3):
    c: Diameter(g0) = 2.1
    c: Distance(g0,g-2) = 4.75
    c: Distance(g0,g-1) = 103.55
FEATURE [PartDesign::Pad] Pad013
  Direction = (0,0,1)
  Length = 0.6
  Length2 = 10
  Placement = pos=(0,0,0.2) rot=(0,0,1;0rad)
  Profile = -> Sketch021
  ReferenceAxis = -> Sketch021 [N_Axis]
  Refine = true
  Type = 0
FEATURE [PartDesign::Body] Body014  label="entretoises010"
  Group = -> [Sketch021,Pad013]
  Origin = -> Origin014
  Tip = -> Pad013
FEATURE [Sketcher::SketchObject] Sketch022
  FullyConstrained = true
  MapMode = 5
  Placement = pos=(0,0,0.2) rot=(0,0,1;0rad)
  sketch-geometry (1):
    g0: Circle CenterX=-4.75 CenterY=-113.65 CenterZ=0 NormalX=0 NormalY=0 NormalZ=1 AngleXU=0 Radius=1.05
  constraints (3):
    c: Diameter(g0) = 2.1
    c: Distance(g0,g-2) = 4.75
    c: Distance(g0,g-1) = 113.65
FEATURE [PartDesign::Pad] Pad014
  Direction = (0,0,1)
  Length = 0.6
  Length2 = 10
  Placement = pos=(0,0,0.2) rot=(0,0,1;0rad)
  Profile = -> Sketch022
  ReferenceAxis = -> Sketch022 [N_Axis]
  Refine = true
  Type = 0
FEATURE [PartDesign::Body] Body015  label="entretoises011"
  Group = -> [Sketch022,Pad014]
  Origin = -> Origin015
  Tip = -> Pad014
FEATURE [Sketcher::SketchObject] Sketch023
  FullyConstrained = true
  MapMode = 5
  Placement = pos=(0,0,0.2) rot=(0,0,1;0rad)
  sketch-geometry (1):
    g0: Circle CenterX=-4.75 CenterY=-123.75 CenterZ=0 NormalX=0 NormalY=0 NormalZ=1 AngleXU=0 Radius=1.05
  constraints (3):
    c: Diameter(g0) = 2.1
    c: Distance(g0,g-2) = 4.75
    c: Distance(g0,g-1) = 123.75
FEATURE [PartDesign::Pad] Pad015
  Direction = (0,0,1)
  Length = 0.6
  Length2 = 10
  Placement = pos=(0,0,0.2) rot=(0,0,1;0rad)
  Profile = -> Sketch023
  ReferenceAxis = -> Sketch023 [N_Axis]
  Refine = true
  Type = 0
FEATURE [PartDesign::Body] Body016  label="entretoises012"
  Group = -> [Sketch023,Pad015]
  Origin = -> Origin016
  Tip = -> Pad015
FEATURE [Sketcher::SketchObject] Sketch024
  FullyConstrained = true
  MapMode = 5
  Placement = pos=(0,0,0.2) rot=(0,0,1;0rad)
  sketch-geometry (1):
    g0: Circle CenterX=-4.75 CenterY=-133.85 CenterZ=0 NormalX=0 NormalY=0 NormalZ=1 AngleXU=0 Radius=1.05
  constraints (3):
    c: Diameter(g0) = 2.1
    c: Distance(g0,g-2) = 4.75
    c: Distance(g0,g-1) = 133.85
FEATURE [PartDesign::Pad] Pad016
  Direction = (0,0,1)
  Length = 0.6
  Length2 = 10
  Placement = pos=(0,0,0.2) rot=(0,0,1;0rad)
  Profile = -> Sketch024
  ReferenceAxis = -> Sketch024 [N_Axis]
  Refine = true
  Type = 0
FEATURE [PartDesign::Body] Body017  label="entretoises013"
  Group = -> [Sketch024,Pad016]
  Origin = -> Origin017
  Tip = -> Pad016
FEATURE [Sketcher::SketchObject] Sketch025
  FullyConstrained = true
  MapMode = 5
  Placement = pos=(0,0,0.2) rot=(0,0,1;0rad)
  sketch-geometry (1):
    g0: Circle CenterX=-4.75 CenterY=-143.95 CenterZ=0 NormalX=0 NormalY=0 NormalZ=1 AngleXU=0 Radius=1.05
  constraints (3):
    c: Diameter(g0) = 2.1
    c: Distance(g0,g-2) = 4.75
    c: Distance(g0,g-1) = 143.95
FEATURE [PartDesign::Pad] Pad017
  Direction = (0,0,1)
  Length = 0.6
  Length2 = 10
  Placement = pos=(0,0,0.2) rot=(0,0,1;0rad)
  Profile = -> Sketch025
  ReferenceAxis = -> Sketch025 [N_Axis]
  Refine = true
  Type = 0
FEATURE [PartDesign::Body] Body018  label="entretoises014"
  Group = -> [Sketch025,Pad017]
  Origin = -> Origin018
  Tip = -> Pad017
FEATURE [Sketcher::SketchObject] Sketch026
  FullyConstrained = true
  MapMode = 5
  Placement = pos=(0,0,0.2) rot=(0,0,1;0rad)
  sketch-geometry (1):
    g0: Circle CenterX=-4.75 CenterY=-154.05 CenterZ=0 NormalX=0 NormalY=0 NormalZ=1 AngleXU=0 Radius=1.05
  constraints (3):
    c: Diameter(g0) = 2.1
    c: Distance(g0,g-2) = 4.75
    c: Distance(g0,g-1) = 154.05
FEATURE [PartDesign::Pad] Pad018
  Direction = (0,0,1)
  Length = 0.6
  Length2 = 10
  Placement = pos=(0,0,0.2) rot=(0,0,1;0rad)
  Profile = -> Sketch026
  ReferenceAxis = -> Sketch026 [N_Axis]
  Refine = true
  Type = 0
FEATURE [PartDesign::Body] Body019  label="entretoises015"
  Group = -> [Sketch026,Pad018]
  Origin = -> Origin019
  Tip = -> Pad018
FEATURE [Sketcher::SketchObject] Sketch027
  FullyConstrained = true
  MapMode = 5
  Placement = pos=(0,0,0.2) rot=(0,0,1;0rad)
  sketch-geometry (1):
    g0: Circle CenterX=-4.75 CenterY=-164.15 CenterZ=0 NormalX=0 NormalY=0 NormalZ=1 AngleXU=0 Radius=1.05
  constraints (3):
    c: Diameter(g0) = 2.1
    c: Distance(g0,g-2) = 4.75
    c: Distance(g0,g-1) = 164.15
FEATURE [PartDesign::Pad] Pad019
  Direction = (0,0,1)
  Length = 0.6
  Length2 = 10
  Placement = pos=(0,0,0.2) rot=(0,0,1;0rad)
  Profile = -> Sketch027
  ReferenceAxis = -> Sketch027 [N_Axis]
  Refine = true
  Type = 0
FEATURE [PartDesign::Body] Body020  label="entretoises016"
  Group = -> [Sketch027,Pad019]
  Origin = -> Origin020
  Tip = -> Pad019
FEATURE [Sketcher::SketchObject] Sketch028
  FullyConstrained = true
  MapMode = 5
  Placement = pos=(0,0,0.2) rot=(0,0,1;0rad)
  sketch-geometry (1):
    g0: Circle CenterX=-4.75 CenterY=-174.25 CenterZ=0 NormalX=0 NormalY=0 NormalZ=1 AngleXU=0 Radius=1.05
  constraints (3):
    c: Diameter(g0) = 2.1
    c: Distance(g0,g-2) = 4.75
    c: Distance(g0,g-1) = 174.25
FEATURE [PartDesign::Pad] Pad020
  Direction = (0,0,1)
  Length = 0.6
  Length2 = 10
  Placement = pos=(0,0,0.2) rot=(0,0,1;0rad)
  Profile = -> Sketch028
  ReferenceAxis = -> Sketch028 [N_Axis]
  Refine = true
  Type = 0
FEATURE [PartDesign::Body] Body021  label="entretoises017"
  Group = -> [Sketch028,Pad020]
  Origin = -> Origin021
  Tip = -> Pad020
FEATURE [Sketcher::SketchObject] Sketch029
  FullyConstrained = true
  MapMode = 5
  Placement = pos=(0,0,0.2) rot=(0,0,1;0rad)
  sketch-geometry (1):
    g0: Circle CenterX=-4.75 CenterY=-184.35 CenterZ=0 NormalX=0 NormalY=0 NormalZ=1 AngleXU=0 Radius=1.05
  constraints (3):
    c: Diameter(g0) = 2.1
    c: Distance(g0,g-2) = 4.75
    c: Distance(g0,g-1) = 184.35
FEATURE [PartDesign::Pad] Pad021
  Direction = (0,0,1)
  Length = 0.6
  Length2 = 10
  Placement = pos=(0,0,0.2) rot=(0,0,1;0rad)
  Profile = -> Sketch029
  ReferenceAxis = -> Sketch029 [N_Axis]
  Refine = true
  Type = 0
FEATURE [PartDesign::Body] Body022  label="entretoises018"
  Group = -> [Sketch029,Pad021]
  Origin = -> Origin022
  Tip = -> Pad021
FEATURE [Sketcher::SketchObject] Sketch030
  FullyConstrained = true
  MapMode = 5
  Placement = pos=(0,0,0.2) rot=(0,0,1;0rad)
  sketch-geometry (1):
    g0: Circle CenterX=-4.75 CenterY=-194.45 CenterZ=0 NormalX=0 NormalY=0 NormalZ=1 AngleXU=0 Radius=1.05
  constraints (3):
    c: Diameter(g0) = 2.1
    c: Distance(g0,g-2) = 4.75
    c: Distance(g0,g-1) = 194.45
FEATURE [PartDesign::Pad] Pad022
  Direction = (0,0,1)
  Length = 0.6
  Length2 = 10
  Placement = pos=(0,0,0.2) rot=(0,0,1;0rad)
  Profile = -> Sketch030
  ReferenceAxis = -> Sketch030 [N_Axis]
  Refine = true
  Type = 0
FEATURE [PartDesign::Body] Body023  label="entretoises019"
  Group = -> [Sketch030,Pad022]
  Origin = -> Origin023
  Tip = -> Pad022
FEATURE [Sketcher::SketchObject] Sketch031
  FullyConstrained = true
  MapMode = 5
  Placement = pos=(0,0,0.2) rot=(0,0,1;0rad)
  sketch-geometry (1):
    g0: Circle CenterX=-4.75 CenterY=-204.55 CenterZ=0 NormalX=0 NormalY=0 NormalZ=1 AngleXU=0 Radius=1.05
  constraints (3):
    c: Diameter(g0) = 2.1
    c: Distance(g0,g-2) = 4.75
    c: Distance(g0,g-1) = 204.55
FEATURE [PartDesign::Pad] Pad023
  Direction = (0,0,1)
  Length = 0.6
  Length2 = 10
  Placement = pos=(0,0,0.2) rot=(0,0,1;0rad)
  Profile = -> Sketch031
  ReferenceAxis = -> Sketch031 [N_Axis]
  Refine = true
  Type = 0
FEATURE [PartDesign::Body] Body024  label="entretoises020"
  Group = -> [Sketch031,Pad023]
  Origin = -> Origin024
  Tip = -> Pad023
FEATURE [Sketcher::SketchObject] Sketch032
  FullyConstrained = true
  MapMode = 5
  Placement = pos=(0,0,0.2) rot=(0,0,1;0rad)
  sketch-geometry (1):
    g0: Circle CenterX=-4.75 CenterY=-214.65 CenterZ=0 NormalX=0 NormalY=0 NormalZ=1 AngleXU=0 Radius=1.05
  constraints (3):
    c: Diameter(g0) = 2.1
    c: Distance(g0,g-2) = 4.75
    c: Distance(g0,g-1) = 214.65
FEATURE [PartDesign::Pad] Pad024
  Direction = (0,0,1)
  Length = 0.6
  Length2 = 10
  Placement = pos=(0,0,0.2) rot=(0,0,1;0rad)
  Profile = -> Sketch032
  ReferenceAxis = -> Sketch032 [N_Axis]
  Refine = true
  Type = 0
FEATURE [PartDesign::Body] Body025  label="entretoises021"
  Group = -> [Sketch032,Pad024]
  Origin = -> Origin025
  Tip = -> Pad024
FEATURE [Sketcher::SketchObject] Sketch033
  FullyConstrained = true
  MapMode = 5
  Placement = pos=(0,0,0.2) rot=(0,0,1;0rad)
  sketch-geometry (1):
    g0: Circle CenterX=-4.75 CenterY=-224.75 CenterZ=0 NormalX=0 NormalY=0 NormalZ=1 AngleXU=0 Radius=1.05
  constraints (3):
    c: Diameter(g0) = 2.1
    c: Distance(g0,g-2) = 4.75
    c: Distance(g0,g-1) = 224.75
FEATURE [PartDesign::Pad] Pad025
  Direction = (0,0,1)
  Length = 0.6
  Length2 = 10
  Placement = pos=(0,0,0.2) rot=(0,0,1;0rad)
  Profile = -> Sketch033
  ReferenceAxis = -> Sketch033 [N_Axis]
  Refine = true
  Type = 0
FEATURE [PartDesign::Body] Body026  label="entretoises022"
  Group = -> [Sketch033,Pad025]
  Origin = -> Origin026
  Tip = -> Pad025
FEATURE [Sketcher::SketchObject] Sketch034
  FullyConstrained = true
  MapMode = 5
  Placement = pos=(0,0,0.2) rot=(0,0,1;0rad)
  sketch-geometry (1):
    g0: Circle CenterX=-4.75 CenterY=-234.85 CenterZ=0 NormalX=0 NormalY=0 NormalZ=1 AngleXU=0 Radius=1.05
  constraints (3):
    c: Diameter(g0) = 2.1
    c: Distance(g0,g-2) = 4.75
    c: Distance(g0,g-1) = 234.85
FEATURE [PartDesign::Pad] Pad026
  Direction = (0,0,1)
  Length = 0.6
  Length2 = 10
  Placement = pos=(0,0,0.2) rot=(0,0,1;0rad)
  Profile = -> Sketch034
  ReferenceAxis = -> Sketch034 [N_Axis]
  Refine = true
  Type = 0
FEATURE [PartDesign::Body] Body027  label="entretoises023"
  Group = -> [Sketch034,Pad026]
  Origin = -> Origin027
  Tip = -> Pad026
FEATURE [Sketcher::SketchObject] Sketch035
  FullyConstrained = true
  MapMode = 5
  Placement = pos=(0,0,0.2) rot=(0,0,1;0rad)
  sketch-geometry (1):
    g0: Circle CenterX=-4.75 CenterY=-244.95 CenterZ=0 NormalX=0 NormalY=0 NormalZ=1 AngleXU=0 Radius=1.05
  constraints (3):
    c: Diameter(g0) = 2.1
    c: Distance(g0,g-2) = 4.75
    c: Distance(g0,g-1) = 244.95
FEATURE [PartDesign::Pad] Pad027
  Direction = (0,0,1)
  Length = 0.6
  Length2 = 10
  Placement = pos=(0,0,0.2) rot=(0,0,1;0rad)
  Profile = -> Sketch035
  ReferenceAxis = -> Sketch035 [N_Axis]
  Refine = true
  Type = 0
FEATURE [PartDesign::Body] Body028  label="entretoises024"
  Group = -> [Sketch035,Pad027]
  Origin = -> Origin028
  Tip = -> Pad027
FEATURE [Sketcher::SketchObject] Sketch036
  FullyConstrained = true
  MapMode = 5
  Placement = pos=(0,0,0.2) rot=(0,0,1;0rad)
  sketch-geometry (1):
    g0: Circle CenterX=-4.75 CenterY=-255.05 CenterZ=0 NormalX=0 NormalY=0 NormalZ=1 AngleXU=0 Radius=1.05
  constraints (3):
    c: Diameter(g0) = 2.1
    c: Distance(g0,g-2) = 4.75
    c: Distance(g0,g-1) = 255.05
FEATURE [PartDesign::Pad] Pad028
  Direction = (0,0,1)
  Length = 0.6
  Length2 = 10
  Placement = pos=(0,0,0.2) rot=(0,0,1;0rad)
  Profile = -> Sketch036
  ReferenceAxis = -> Sketch036 [N_Axis]
  Refine = true
  Type = 0
FEATURE [PartDesign::Body] Body029  label="entretoises025"
  Group = -> [Sketch036,Pad028]
  Origin = -> Origin029
  Tip = -> Pad028
FEATURE [Sketcher::SketchObject] Sketch037
  FullyConstrained = true
  MapMode = 5
  Placement = pos=(0,0,0.2) rot=(0,0,1;0rad)
  sketch-geometry (1):
    g0: Circle CenterX=-4.75 CenterY=-265.15 CenterZ=0 NormalX=0 NormalY=0 NormalZ=1 AngleXU=0 Radius=1.05
  constraints (3):
    c: Diameter(g0) = 2.1
    c: Distance(g0,g-2) = 4.75
    c: Distance(g0,g-1) = 265.15
FEATURE [PartDesign::Pad] Pad029
  Direction = (0,0,1)
  Length = 0.6
  Length2 = 10
  Placement = pos=(0,0,0.2) rot=(0,0,1;0rad)
  Profile = -> Sketch037
  ReferenceAxis = -> Sketch037 [N_Axis]
  Refine = true
  Type = 0
FEATURE [PartDesign::Body] Body030  label="entretoises026"
  Group = -> [Sketch037,Pad029]
  Origin = -> Origin030
  Tip = -> Pad029
FEATURE [Sketcher::SketchObject] Sketch038
  FullyConstrained = true
  MapMode = 5
  Placement = pos=(0,0,0.2) rot=(0,0,1;0rad)
  sketch-geometry (1):
    g0: Circle CenterX=-4.75 CenterY=-275.25 CenterZ=0 NormalX=0 NormalY=0 NormalZ=1 AngleXU=0 Radius=1.05
  constraints (3):
    c: Diameter(g0) = 2.1
    c: Distance(g0,g-2) = 4.75
    c: Distance(g0,g-1) = 275.25
FEATURE [PartDesign::Pad] Pad030
  Direction = (0,0,1)
  Length = 0.6
  Length2 = 10
  Placement = pos=(0,0,0.2) rot=(0,0,1;0rad)
  Profile = -> Sketch038
  ReferenceAxis = -> Sketch038 [N_Axis]
  Refine = true
  Type = 0
FEATURE [PartDesign::Body] Body031  label="entretoises027"
  Group = -> [Sketch038,Pad030]
  Origin = -> Origin031
  Tip = -> Pad030
FEATURE [Sketcher::SketchObject] Sketch039
  FullyConstrained = true
  MapMode = 5
  Placement = pos=(0,0,0.2) rot=(0,0,1;0rad)
  sketch-geometry (1):
    g0: Circle CenterX=-4.75 CenterY=-285.35 CenterZ=0 NormalX=0 NormalY=0 NormalZ=1 AngleXU=0 Radius=1.05
  constraints (3):
    c: Diameter(g0) = 2.1
    c: Distance(g0,g-2) = 4.75
    c: Distance(g0,g-1) = 285.35
FEATURE [PartDesign::Pad] Pad031
  Direction = (0,0,1)
  Length = 0.6
  Length2 = 10
  Placement = pos=(0,0,0.2) rot=(0,0,1;0rad)
  Profile = -> Sketch039
  ReferenceAxis = -> Sketch039 [N_Axis]
  Refine = true
  Type = 0
FEATURE [PartDesign::Body] Body032  label="entretoises028"
  Group = -> [Sketch039,Pad031]
  Origin = -> Origin032
  Tip = -> Pad031
FEATURE [Sketcher::SketchObject] Sketch040
  FullyConstrained = true
  MapMode = 5
  Placement = pos=(0,0,0.2) rot=(0,0,1;0rad)
  sketch-geometry (1):
    g0: Circle CenterX=-4.75 CenterY=-295.45 CenterZ=0 NormalX=0 NormalY=0 NormalZ=1 AngleXU=0 Radius=1.05
  constraints (3):
    c: Diameter(g0) = 2.1
    c: Distance(g0,g-2) = 4.75
    c: Distance(g0,g-1) = 295.45
FEATURE [PartDesign::Pad] Pad032
  Direction = (0,0,1)
  Length = 0.6
  Length2 = 10
  Placement = pos=(0,0,0.2) rot=(0,0,1;0rad)
  Profile = -> Sketch040
  ReferenceAxis = -> Sketch040 [N_Axis]
  Refine = true
  Type = 0
FEATURE [PartDesign::Body] Body033  label="entretoises029"
  Group = -> [Sketch040,Pad032]
  Origin = -> Origin033
  Tip = -> Pad032
FEATURE [Sketcher::SketchObject] Sketch041
  FullyConstrained = true
  MapMode = 5
  Placement = pos=(0,0,0.2) rot=(0,0,1;0rad)
  sketch-geometry (1):
    g0: Circle CenterX=-4.75 CenterY=-305.55 CenterZ=0 NormalX=0 NormalY=0 NormalZ=1 AngleXU=0 Radius=1.05
  constraints (3):
    c: Diameter(g0) = 2.1
    c: Distance(g0,g-2) = 4.75
    c: Distance(g0,g-1) = 305.55
FEATURE [PartDesign::Pad] Pad033
  Direction = (0,0,1)
  Length = 0.6
  Length2 = 10
  Placement = pos=(0,0,0.2) rot=(0,0,1;0rad)
  Profile = -> Sketch041
  ReferenceAxis = -> Sketch041 [N_Axis]
  Refine = true
  Type = 0
FEATURE [PartDesign::Body] Body034  label="entretoises030"
  Group = -> [Sketch041,Pad033]
  Origin = -> Origin034
  Tip = -> Pad033
FEATURE [Sketcher::SketchObject] Sketch042
  FullyConstrained = true
  MapMode = 5
  Placement = pos=(0,0,0.2) rot=(0,0,1;0rad)
  sketch-geometry (1):
    g0: Circle CenterX=-4.75 CenterY=-315.65 CenterZ=0 NormalX=0 NormalY=0 NormalZ=1 AngleXU=0 Radius=1.05
  constraints (3):
    c: Diameter(g0) = 2.1
    c: Distance(g0,g-2) = 4.75
    c: Distance(g0,g-1) = 315.65
FEATURE [PartDesign::Pad] Pad034
  Direction = (0,0,1)
  Length = 0.6
  Length2 = 10
  Placement = pos=(0,0,0.2) rot=(0,0,1;0rad)
  Profile = -> Sketch042
  ReferenceAxis = -> Sketch042 [N_Axis]
  Refine = true
  Type = 0
FEATURE [PartDesign::Body] Body035  label="entretoises031"
  Group = -> [Sketch042,Pad034]
  Origin = -> Origin035
  Tip = -> Pad034
FEATURE [Sketcher::SketchObject] Sketch043
  FullyConstrained = true
  MapMode = 5
  Placement = pos=(0,0,0.2) rot=(0,0,1;0rad)
  sketch-geometry (1):
    g0: Circle CenterX=-4.75 CenterY=-325.75 CenterZ=0 NormalX=0 NormalY=0 NormalZ=1 AngleXU=0 Radius=1.05
  constraints (3):
    c: Diameter(g0) = 2.1
    c: Distance(g0,g-2) = 4.75
    c: Distance(g0,g-1) = 325.75
FEATURE [PartDesign::Pad] Pad035
  Direction = (0,0,1)
  Length = 0.6
  Length2 = 10
  Placement = pos=(0,0,0.2) rot=(0,0,1;0rad)
  Profile = -> Sketch043
  ReferenceAxis = -> Sketch043 [N_Axis]
  Refine = true
  Type = 0
FEATURE [PartDesign::Body] Body036  label="entretoises032"
  Group = -> [Sketch043,Pad035]
  Origin = -> Origin036
  Tip = -> Pad035
FEATURE [Sketcher::SketchObject] Sketch044
  FullyConstrained = true
  MapMode = 5
  Placement = pos=(0,0,0.2) rot=(0,0,1;0rad)
  sketch-geometry (1):
    g0: Circle CenterX=-4.75 CenterY=-335.85 CenterZ=0 NormalX=0 NormalY=0 NormalZ=1 AngleXU=0 Radius=1.05
  constraints (3):
    c: Diameter(g0) = 2.1
    c: Distance(g0,g-2) = 4.75
    c: Distance(g0,g-1) = 335.85
FEATURE [PartDesign::Pad] Pad036
  Direction = (0,0,1)
  Length = 0.6
  Length2 = 10
  Placement = pos=(0,0,0.2) rot=(0,0,1;0rad)
  Profile = -> Sketch044
  ReferenceAxis = -> Sketch044 [N_Axis]
  Refine = true
  Type = 0
FEATURE [PartDesign::Body] Body037  label="entretoises033"
  Group = -> [Sketch044,Pad036]
  Origin = -> Origin037
  Tip = -> Pad036
FEATURE [Sketcher::SketchObject] Sketch045
  FullyConstrained = true
  MapMode = 5
  Placement = pos=(0,0,0.2) rot=(0,0,1;0rad)
  sketch-geometry (1):
    g0: Circle CenterX=-4.75 CenterY=-345.95 CenterZ=0 NormalX=0 NormalY=0 NormalZ=1 AngleXU=0 Radius=1.05
  constraints (3):
    c: Diameter(g0) = 2.1
    c: Distance(g0,g-2) = 4.75
    c: Distance(g0,g-1) = 345.95
FEATURE [PartDesign::Pad] Pad037
  Direction = (0,0,1)
  Length = 0.6
  Length2 = 10
  Placement = pos=(0,0,0.2) rot=(0,0,1;0rad)
  Profile = -> Sketch045
  ReferenceAxis = -> Sketch045 [N_Axis]
  Refine = true
  Type = 0
FEATURE [PartDesign::Body] Body038  label="entretoises034"
  Group = -> [Sketch045,Pad037]
  Origin = -> Origin038
  Tip = -> Pad037
FEATURE [Sketcher::SketchObject] Sketch046
  FullyConstrained = true
  MapMode = 5
  Placement = pos=(0,0,0.2) rot=(0,0,1;0rad)
  sketch-geometry (1):
    g0: Circle CenterX=-4.75 CenterY=-356.05 CenterZ=0 NormalX=0 NormalY=0 NormalZ=1 AngleXU=0 Radius=1.05
  constraints (3):
    c: Diameter(g0) = 2.1
    c: Distance(g0,g-2) = 4.75
    c: Distance(g0,g-1) = 356.05
FEATURE [PartDesign::Pad] Pad038
  Direction = (0,0,1)
  Length = 0.6
  Length2 = 10
  Placement = pos=(0,0,0.2) rot=(0,0,1;0rad)
  Profile = -> Sketch046
  ReferenceAxis = -> Sketch046 [N_Axis]
  Refine = true
  Type = 0
FEATURE [PartDesign::Body] Body039  label="entretoises035"
  Group = -> [Sketch046,Pad038]
  Origin = -> Origin039
  Tip = -> Pad038
FEATURE [Sketcher::SketchObject] Sketch047
  FullyConstrained = true
  MapMode = 5
  Placement = pos=(0,0,0.2) rot=(0,0,1;0rad)
  sketch-geometry (1):
    g0: Circle CenterX=-4.75 CenterY=-366.15 CenterZ=0 NormalX=0 NormalY=0 NormalZ=1 AngleXU=0 Radius=1.05
  constraints (3):
    c: Diameter(g0) = 2.1
    c: Distance(g0,g-2) = 4.75
    c: Distance(g0,g-1) = 366.15
FEATURE [PartDesign::Pad] Pad039
  Direction = (0,0,1)
  Length = 0.6
  Length2 = 10
  Placement = pos=(0,0,0.2) rot=(0,0,1;0rad)
  Profile = -> Sketch047
  ReferenceAxis = -> Sketch047 [N_Axis]
  Refine = true
  Type = 0
FEATURE [PartDesign::Body] Body040  label="entretoises036"
  Group = -> [Sketch047,Pad039]
  Origin = -> Origin040
  Tip = -> Pad039
FEATURE [Sketcher::SketchObject] Sketch048
  FullyConstrained = true
  MapMode = 5
  Placement = pos=(0,0,0.2) rot=(0,0,1;0rad)
  sketch-geometry (1):
    g0: Circle CenterX=-4.75 CenterY=-376.25 CenterZ=0 NormalX=0 NormalY=0 NormalZ=1 AngleXU=0 Radius=1.05
  constraints (3):
    c: Diameter(g0) = 2.1
    c: Distance(g0,g-2) = 4.75
    c: Distance(g0,g-1) = 376.25
FEATURE [PartDesign::Pad] Pad040
  Direction = (0,0,1)
  Length = 0.6
  Length2 = 10
  Placement = pos=(0,0,0.2) rot=(0,0,1;0rad)
  Profile = -> Sketch048
  ReferenceAxis = -> Sketch048 [N_Axis]
  Refine = true
  Type = 0
FEATURE [PartDesign::Body] Body041  label="entretoises037"
  Group = -> [Sketch048,Pad040]
  Origin = -> Origin041
  Tip = -> Pad040
FEATURE [Sketcher::SketchObject] Sketch049
  FullyConstrained = true
  MapMode = 5
  Placement = pos=(0,0,0.2) rot=(0,0,1;0rad)
  sketch-geometry (1):
    g0: Circle CenterX=-4.75 CenterY=-386.35 CenterZ=0 NormalX=0 NormalY=0 NormalZ=1 AngleXU=0 Radius=1.05
  constraints (3):
    c: Diameter(g0) = 2.1
    c: Distance(g0,g-2) = 4.75
    c: Distance(g0,g-1) = 386.35
FEATURE [PartDesign::Pad] Pad041
  Direction = (0,0,1)
  Length = 0.6
  Length2 = 10
  Placement = pos=(0,0,0.2) rot=(0,0,1;0rad)
  Profile = -> Sketch049
  ReferenceAxis = -> Sketch049 [N_Axis]
  Refine = true
  Type = 0
FEATURE [PartDesign::Body] Body042  label="entretoises038"
  Group = -> [Sketch049,Pad041]
  Origin = -> Origin042
  Tip = -> Pad041
FEATURE [Sketcher::SketchObject] Sketch050
  FullyConstrained = true
  MapMode = 5
  Placement = pos=(0,0,0.2) rot=(0,0,1;0rad)
  sketch-geometry (1):
    g0: Circle CenterX=-4.75 CenterY=-396.45 CenterZ=0 NormalX=0 NormalY=0 NormalZ=1 AngleXU=0 Radius=1.05
  constraints (3):
    c: Diameter(g0) = 2.1
    c: Distance(g0,g-2) = 4.75
    c: Distance(g0,g-1) = 396.45
FEATURE [PartDesign::Pad] Pad042
  Direction = (0,0,1)
  Length = 0.6
  Length2 = 10
  Placement = pos=(0,0,0.2) rot=(0,0,1;0rad)
  Profile = -> Sketch050
  ReferenceAxis = -> Sketch050 [N_Axis]
  Refine = true
  Type = 0
FEATURE [PartDesign::Body] Body043  label="entretoises039"
  Group = -> [Sketch050,Pad042]
  Origin = -> Origin043
  Tip = -> Pad042
FEATURE [Sketcher::SketchObject] Sketch051
  FullyConstrained = true
  MapMode = 5
  Placement = pos=(0,0,0.2) rot=(0,0,1;0rad)
  sketch-geometry (1):
    g0: Circle CenterX=-4.75 CenterY=-406.55 CenterZ=0 NormalX=0 NormalY=0 NormalZ=1 AngleXU=0 Radius=1.05
  constraints (3):
    c: Diameter(g0) = 2.1
    c: Distance(g0,g-2) = 4.75
    c: Distance(g0,g-1) = 406.55
FEATURE [PartDesign::Pad] Pad043
  Direction = (0,0,1)
  Length = 0.6
  Length2 = 10
  Placement = pos=(0,0,0.2) rot=(0,0,1;0rad)
  Profile = -> Sketch051
  ReferenceAxis = -> Sketch051 [N_Axis]
  Refine = true
  Type = 0
FEATURE [PartDesign::Body] Body044  label="entretoises040"
  Group = -> [Sketch051,Pad043]
  Origin = -> Origin044
  Tip = -> Pad043
FEATURE [Sketcher::SketchObject] Sketch052
  FullyConstrained = true
  MapMode = 5
  Placement = pos=(0,0,0.2) rot=(0,0,1;0rad)
  sketch-geometry (1):
    g0: Circle CenterX=-4.75 CenterY=-416.65 CenterZ=0 NormalX=0 NormalY=0 NormalZ=1 AngleXU=0 Radius=1.05
  constraints (3):
    c: Diameter(g0) = 2.1
    c: Distance(g0,g-2) = 4.75
    c: Distance(g0,g-1) = 416.65
FEATURE [PartDesign::Pad] Pad044
  Direction = (0,0,1)
  Length = 0.6
  Length2 = 10
  Placement = pos=(0,0,0.2) rot=(0,0,1;0rad)
  Profile = -> Sketch052
  ReferenceAxis = -> Sketch052 [N_Axis]
  Refine = true
  Type = 0
FEATURE [PartDesign::Body] Body045  label="entretoises041"
  Group = -> [Sketch052,Pad044]
  Origin = -> Origin045
  Tip = -> Pad044
FEATURE [Sketcher::SketchObject] Sketch053
  FullyConstrained = true
  MapMode = 5
  Placement = pos=(0,0,0.2) rot=(0,0,1;0rad)
  sketch-geometry (1):
    g0: Circle CenterX=-4.75 CenterY=-426.75 CenterZ=0 NormalX=0 NormalY=0 NormalZ=1 AngleXU=0 Radius=1.05
  constraints (3):
    c: Diameter(g0) = 2.1
    c: Distance(g0,g-2) = 4.75
    c: Distance(g0,g-1) = 426.75
FEATURE [PartDesign::Pad] Pad045
  Direction = (0,0,1)
  Length = 0.6
  Length2 = 10
  Placement = pos=(0,0,0.2) rot=(0,0,1;0rad)
  Profile = -> Sketch053
  ReferenceAxis = -> Sketch053 [N_Axis]
  Refine = true
  Type = 0
FEATURE [PartDesign::Body] Body046  label="entretoises042"
  Group = -> [Sketch053,Pad045]
  Origin = -> Origin046
  Tip = -> Pad045
FEATURE [Sketcher::SketchObject] Sketch054
  FullyConstrained = true
  MapMode = 5
  Placement = pos=(0,0,0.2) rot=(0,0,1;0rad)
  sketch-geometry (1):
    g0: Circle CenterX=-4.75 CenterY=-436.85 CenterZ=0 NormalX=0 NormalY=0 NormalZ=1 AngleXU=0 Radius=1.05
  constraints (3):
    c: Diameter(g0) = 2.1
    c: Distance(g0,g-2) = 4.75
    c: Distance(g0,g-1) = 436.85
FEATURE [PartDesign::Pad] Pad046
  Direction = (0,0,1)
  Length = 0.6
  Length2 = 10
  Placement = pos=(0,0,0.2) rot=(0,0,1;0rad)
  Profile = -> Sketch054
  ReferenceAxis = -> Sketch054 [N_Axis]
  Refine = true
  Type = 0
FEATURE [PartDesign::Body] Body047  label="entretoises043"
  Group = -> [Sketch054,Pad046]
  Origin = -> Origin047
  Tip = -> Pad046
FEATURE [Sketcher::SketchObject] Sketch055
  FullyConstrained = true
  MapMode = 5
  Placement = pos=(0,0,0.2) rot=(0,0,1;0rad)
  sketch-geometry (1):
    g0: Circle CenterX=-4.75 CenterY=-457.05 CenterZ=0 NormalX=0 NormalY=0 NormalZ=1 AngleXU=0 Radius=1.05
  constraints (3):
    c: Diameter(g0) = 2.1
    c: Distance(g0,g-2) = 4.75
    c: Distance(g0,g-1) = 457.05
FEATURE [PartDesign::Pad] Pad047
  Direction = (0,0,1)
  Length = 0.6
  Length2 = 10
  Placement = pos=(0,0,0.2) rot=(0,0,1;0rad)
  Profile = -> Sketch055
  ReferenceAxis = -> Sketch055 [N_Axis]
  Refine = true
  Type = 0
FEATURE [PartDesign::Body] Body048  label="entretoises044"
  Group = -> [Sketch055,Pad047]
  Origin = -> Origin048
  Tip = -> Pad047
FEATURE [PartDesign::Pad] Pad009
  Direction = (0,0,1)
  Length = 0.6
  Length2 = 10
  Placement = pos=(0,0,0.2) rot=(0,0,1;0rad)
  Profile = -> Sketch017
  ReferenceAxis = -> Sketch017 [N_Axis]
  Refine = true
  Type = 0
FEATURE [PartDesign::Body] Body010  label="entretoises006"
  Group = -> [Sketch017,Pad009]
  Origin = -> Origin010
  Tip = -> Pad009
FEATURE [Sketcher::SketchObject] Sketch056
  FullyConstrained = true
  MapMode = 5
  Placement = pos=(0,0,0.2) rot=(0,0,1;0rad)
  sketch-geometry (1):
    g0: Circle CenterX=-4.75 CenterY=-467.15 CenterZ=0 NormalX=0 NormalY=0 NormalZ=1 AngleXU=0 Radius=1.05
  constraints (3):
    c: Diameter(g0) = 2.1
    c: Distance(g0,g-2) = 4.75
    c: Distance(g0,g-1) = 467.15
FEATURE [PartDesign::Pad] Pad048
  Direction = (0,0,1)
  Length = 0.6
  Length2 = 10
  Placement = pos=(0,0,0.2) rot=(0,0,1;0rad)
  Profile = -> Sketch056
  ReferenceAxis = -> Sketch056 [N_Axis]
  Refine = true
  Type = 0
FEATURE [PartDesign::Body] Body049  label="entretoises045"
  Group = -> [Sketch056,Pad048]
  Origin = -> Origin049
  Tip = -> Pad048
FEATURE [Sketcher::SketchObject] Sketch057
  FullyConstrained = true
  MapMode = 5
  Placement = pos=(0,0,0.2) rot=(0,0,1;0rad)
  sketch-geometry (1):
    g0: Circle CenterX=-4.75 CenterY=-477.25 CenterZ=0 NormalX=0 NormalY=0 NormalZ=1 AngleXU=0 Radius=1.05
  constraints (3):
    c: Diameter(g0) = 2.1
    c: Distance(g0,g-2) = 4.75
    c: Distance(g0,g-1) = 477.25
FEATURE [PartDesign::Pad] Pad049
  Direction = (0,0,1)
  Length = 0.6
  Length2 = 10
  Placement = pos=(0,0,0.2) rot=(0,0,1;0rad)
  Profile = -> Sketch057
  ReferenceAxis = -> Sketch057 [N_Axis]
  Refine = true
  Type = 0
FEATURE [PartDesign::Body] Body050  label="entretoises046"
  Group = -> [Sketch057,Pad049]
  Origin = -> Origin050
  Tip = -> Pad049
FEATURE [Sketcher::SketchObject] Sketch058
  FullyConstrained = true
  MapMode = 5
  Placement = pos=(0,0,0.2) rot=(0,0,1;0rad)
  sketch-geometry (1):
    g0: Circle CenterX=-4.75 CenterY=-487.35 CenterZ=0 NormalX=0 NormalY=0 NormalZ=1 AngleXU=0 Radius=1.05
  constraints (3):
    c: Diameter(g0) = 2.1
    c: Distance(g0,g-2) = 4.75
    c: Distance(g0,g-1) = 487.35
FEATURE [PartDesign::Pad] Pad050
  Direction = (0,0,1)
  Length = 0.6
  Length2 = 10
  Placement = pos=(0,0,0.2) rot=(0,0,1;0rad)
  Profile = -> Sketch058
  ReferenceAxis = -> Sketch058 [N_Axis]
  Refine = true
  Type = 0
FEATURE [PartDesign::Body] Body051  label="entretoises047"
  Group = -> [Sketch058,Pad050]
  Origin = -> Origin051
  Tip = -> Pad050
FEATURE [Sketcher::SketchObject] Sketch059
  FullyConstrained = true
  MapMode = 5
  Placement = pos=(0,0,0.2) rot=(0,0,1;0rad)
  sketch-geometry (1):
    g0: Circle CenterX=-4.75 CenterY=-446.95 CenterZ=0 NormalX=0 NormalY=0 NormalZ=1 AngleXU=0 Radius=1.05
  constraints (3):
    c: Diameter(g0) = 2.1
    c: Distance(g0,g-2) = 4.75
    c: Distance(g0,g-1) = 446.95
FEATURE [PartDesign::Pad] Pad051
  Direction = (0,0,1)
  Length = 0.6
  Length2 = 10
  Placement = pos=(0,0,0.2) rot=(0,0,1;0rad)
  Profile = -> Sketch059
  ReferenceAxis = -> Sketch059 [N_Axis]
  Refine = true
  Type = 0
FEATURE [PartDesign::Body] Body052  label="entretoises048"
  Group = -> [Sketch059,Pad051]
  Origin = -> Origin052
  Tip = -> Pad051
FEATURE [App::DocumentObjectGroup] Group  label="cadre gauche"
  Group = -> [Body052,Body051,Body050,Body040,Body041,Body042,Body043,Body044,Body045,Body046,Body047,Body048,Body049,Body026,Body027,Body028,Body029,Body030,Body031,Body032,Body033,Body034,Body035,Body036,Body037,Body038,Body039,Body015,Body016,Body017,Body018,Body019,Body020,Body021,Body022,Body023,Body024,Body025,Body006,Body007,Body008,Body009,Body010,Body011,Body012,Body013,Body014,Body,Body001,Body002,+3 more]
FEATURE [Part::Feature] Group001  label="cadre droite"
  Placement = pos=(1000,-500,0) rot=(0,0,1;3.14159rad)
  shape: bbox 9.501 x 500 x 1.001 mm, 263 faces, 51 solids (baked)
FEATURE [PartDesign::Body] Body055  label="percage pour rivet 7340a 2/3mm de structure001"
  Origin = -> Origin055
  Placement = pos=(504.546,-15.4212,0) rot=(0,0,1;4.71239rad)
FEATURE [Sketcher::SketchObject] Sketch060
  FullyConstrained = false
  MapMode = 5
  Placement = pos=(0,0,0) rot=(0.57735,0.57735,0.57735;2.0944rad)
  sketch-geometry (3):
    g0: LineSegment StartX=0 StartY=-2.13969e-08 StartZ=0 EndX=0 EndY=9.5 EndZ=0
    g1: LineSegment StartX=-1.06984e-08 StartY=9.5 StartZ=0 EndX=-9.5 EndY=0 EndZ=0
    g2: LineSegment StartX=-9.5 StartY=0 StartZ=0 EndX=0 EndY=0 EndZ=0
  constraints (5):
    c: Vertical(g0)
    c: Horizontal(g2)
    c: DistanceX(g2,g2) = 9.5
    c: DistanceY(g0,g0) = 9.5
    c: Angle(g2,g1) = 0.785398
FEATURE [Sketcher::SketchObject] Sketch061
  FullyConstrained = true
  MapMode = 5
  Placement = pos=(0,0,0) rot=(1,0,0;1.5708rad)
  sketch-geometry (8):
    g0: LineSegment StartX=0 StartY=0 StartZ=0 EndX=0 EndY=9.5 EndZ=0
    g1: LineSegment StartX=0 StartY=9.5 StartZ=0 EndX=1 EndY=9.5 EndZ=0
    g2: LineSegment StartX=1 StartY=9.5 StartZ=0 EndX=1 EndY=0 EndZ=0
    g3: LineSegment StartX=1 StartY=0 StartZ=0 EndX=0.8 EndY=0 EndZ=0
    g4: LineSegment StartX=0 StartY=0 StartZ=0 EndX=0.2 EndY=0 EndZ=0
    g5: LineSegment StartX=0.2 StartY=0 StartZ=0 EndX=0.2 EndY=9.3 EndZ=0
    g6: LineSegment StartX=0.2 StartY=9.3 StartZ=0 EndX=0.8 EndY=9.3 EndZ=0
    g7: LineSegment StartX=0.8 StartY=9.3 StartZ=0 EndX=0.8 EndY=0 EndZ=0
  constraints (23):
    c: Coincident(g0,g-1)
    c: PointOnObject(g0,g-2)
    c: Coincident(g1,g0)
    c: Horizontal(g1)
    c: Coincident(g2,g1)
    c: Vertical(g2)
    c: Coincident(g3,g2)
    c: Horizontal(g3)
    c: DistanceY(g2,g2) = 9.5
    c: DistanceY(g0,g0) = 9.5
    c: Coincident(g4,g0)
    c: PointOnObject(g4,g-1)
    c: Coincident(g5,g4)
    c: Vertical(g5)
    c: Coincident(g6,g5)
    c: Horizontal(g6)
    c: Coincident(g7,g6)
    c: Coincident(g7,g3)
    c: Vertical(g7)
    c: DistanceX(g1,g1) = 1
    c: DistanceX(g6,g6) = 0.6
    c: DistanceX(g4,g4) = 0.2
    c: DistanceY(g5,g5) = 9.3
FEATURE [PartDesign::Pad] Pad052
  Direction = (0,-1,2e-16)
  Length = 500
  Length2 = 10
  Placement = pos=(0,0,0) rot=(1,0,0;1.5708rad)
  Profile = -> Sketch061
  ReferenceAxis = -> Sketch061 [N_Axis]
  Type = 0
FEATURE [PartDesign::Pocket] Pocket004
  BaseFeature = -> Pad052
  Direction = (-1,-1e-16,1e-16)
  Length = 5
  Length2 = 5
  Placement = pos=(0,0,0) rot=(1,0,0;1.5708rad)
  Profile = -> Sketch060
  ReferenceAxis = -> Sketch060 [N_Axis]
  Reversed = true
  Type = 1
FEATURE [Sketcher::SketchObject] Sketch062
  FullyConstrained = false
  MapMode = 5
  Placement = pos=(0,0,0) rot=(0.57735,0.57735,0.57735;2.0944rad)
  sketch-geometry (3):
    g0: LineSegment StartX=-500 StartY=0 StartZ=0 EndX=-490.5 EndY=0 EndZ=0
    g1: LineSegment StartX=-500 StartY=0 StartZ=0 EndX=-500 EndY=9.5 EndZ=0
    g2: LineSegment StartX=-490.5 StartY=0 StartZ=0 EndX=-500 EndY=9.5 EndZ=0
  constraints (7):
    c: Horizontal(g0)
    c: DistanceX(g0,g0) = 9.5
    c: Coincident(g1,g0)
    c: Vertical(g1)
    c: Coincident(g2,g0)
    c: Coincident(g2,g1)
    c: DistanceY(g1,g1) = 9.5
FEATURE [PartDesign::Pocket] Pocket005  label="cadre découoé001"
  BaseFeature = -> Pocket004
  Direction = (-1,-1e-16,1e-16)
  Length = 5
  Length2 = 5
  Placement = pos=(0,0,0) rot=(1,0,0;1.5708rad)
  Profile = -> Sketch062
  ReferenceAxis = -> Sketch062 [N_Axis]
  Reversed = true
  Type = 1
FEATURE [PartDesign::Body] Body053  label="cadre gauche alu001"
  Group = -> [Sketch061,Pad052,Sketch060,Pocket004,Sketch062,Pocket005]
  Origin = -> Origin053
  Placement = pos=(504.546,-15.4212,0) rot=(0.57735,0.57735,0.57735;4.18879rad)
  Tip = -> Pocket005
FEATURE [Sketcher::SketchObject] Sketch063
  FullyConstrained = true
  MapMode = 5
  sketch-geometry (48):
    g0: Circle CenterX=-4.75 CenterY=-487.35 CenterZ=0 NormalX=0 NormalY=0 NormalZ=1 AngleXU=0 Radius=1.05
    g1: Circle CenterX=-4.75 CenterY=-477.25 CenterZ=0 NormalX=0 NormalY=0 NormalZ=1 AngleXU=0 Radius=1.05
    g2: Circle CenterX=-4.75 CenterY=-457.05 CenterZ=0 NormalX=0 NormalY=0 NormalZ=1 AngleXU=0 Radius=1.05
    g3: Circle CenterX=-4.75 CenterY=-467.15 CenterZ=0 NormalX=0 NormalY=0 NormalZ=1 AngleXU=0 Radius=1.05
    g4: Circle CenterX=-4.75 CenterY=-416.65 CenterZ=0 NormalX=0 NormalY=0 NormalZ=1 AngleXU=0 Radius=1.05
    g5: Circle CenterX=-4.75 CenterY=-426.75 CenterZ=0 NormalX=0 NormalY=0 NormalZ=1 AngleXU=0 Radius=1.05
    g6: Circle CenterX=-4.75 CenterY=-436.85 CenterZ=0 NormalX=0 NormalY=0 NormalZ=1 AngleXU=0 Radius=1.05
    g7: Circle CenterX=-4.75 CenterY=-446.95 CenterZ=0 NormalX=0 NormalY=0 NormalZ=1 AngleXU=0 Radius=1.05
    g8: Circle CenterX=-4.75 CenterY=-335.85 CenterZ=0 NormalX=0 NormalY=0 NormalZ=1 AngleXU=0 Radius=1.05
    g9: Circle CenterX=-4.75 CenterY=-345.95 CenterZ=0 NormalX=0 NormalY=0 NormalZ=1 AngleXU=0 Radius=1.05
    g10: Circle CenterX=-4.75 CenterY=-356.05 CenterZ=0 NormalX=0 NormalY=0 NormalZ=1 AngleXU=0 Radius=1.05
    g11: Circle CenterX=-4.75 CenterY=-366.15 CenterZ=0 NormalX=0 NormalY=0 NormalZ=1 AngleXU=0 Radius=1.05
    g12: Circle CenterX=-4.75 CenterY=-376.25 CenterZ=0 NormalX=0 NormalY=0 NormalZ=1 AngleXU=0 Radius=1.05
    g13: Circle CenterX=-4.75 CenterY=-386.35 CenterZ=0 NormalX=0 NormalY=0 NormalZ=1 AngleXU=0 Radius=1.05
    g14: Circle CenterX=-4.75 CenterY=-396.45 CenterZ=0 NormalX=0 NormalY=0 NormalZ=1 AngleXU=0 Radius=1.05
    g15: Circle CenterX=-4.75 CenterY=-406.55 CenterZ=0 NormalX=0 NormalY=0 NormalZ=1 AngleXU=0 Radius=1.05
    g16: Circle CenterX=-4.75 CenterY=-174.25 CenterZ=0 NormalX=0 NormalY=0 NormalZ=1 AngleXU=0 Radius=1.05
    g17: Circle CenterX=-4.75 CenterY=-184.35 CenterZ=0 NormalX=0 NormalY=0 NormalZ=1 AngleXU=0 Radius=1.05
    g18: Circle CenterX=-4.75 CenterY=-194.45 CenterZ=0 NormalX=0 NormalY=0 NormalZ=1 AngleXU=0 Radius=1.05
    g19: Circle CenterX=-4.75 CenterY=-204.55 CenterZ=0 NormalX=0 NormalY=0 NormalZ=1 AngleXU=0 Radius=1.05
    g20: Circle CenterX=-4.75 CenterY=-214.65 CenterZ=0 NormalX=0 NormalY=0 NormalZ=1 AngleXU=0 Radius=1.05
    g21: Circle CenterX=-4.75 CenterY=-224.75 CenterZ=0 NormalX=0 NormalY=0 NormalZ=1 AngleXU=0 Radius=1.05
    g22: Circle CenterX=-4.75 CenterY=-234.85 CenterZ=0 NormalX=0 NormalY=0 NormalZ=1 AngleXU=0 Radius=1.05
    g23: Circle CenterX=-4.75 CenterY=-244.95 CenterZ=0 NormalX=0 NormalY=0 NormalZ=1 AngleXU=0 Radius=1.05
    g24: Circle CenterX=-4.75 CenterY=-255.05 CenterZ=0 NormalX=0 NormalY=0 NormalZ=1 AngleXU=0 Radius=1.05
    g25: Circle CenterX=-4.75 CenterY=-265.15 CenterZ=0 NormalX=0 NormalY=0 NormalZ=1 AngleXU=0 Radius=1.05
    g26: Circle CenterX=-4.75 CenterY=-275.25 CenterZ=0 NormalX=0 NormalY=0 NormalZ=1 AngleXU=0 Radius=1.05
    g27: Circle CenterX=-4.75 CenterY=-285.35 CenterZ=0 NormalX=0 NormalY=0 NormalZ=1 AngleXU=0 Radius=1.05
    g28: Circle CenterX=-4.75 CenterY=-295.45 CenterZ=0 NormalX=0 NormalY=0 NormalZ=1 AngleXU=0 Radius=1.05
    g29: Circle CenterX=-4.75 CenterY=-305.55 CenterZ=0 NormalX=0 NormalY=0 NormalZ=1 AngleXU=0 Radius=1.05
    g30: Circle CenterX=-4.75 CenterY=-315.65 CenterZ=0 NormalX=0 NormalY=0 NormalZ=1 AngleXU=0 Radius=1.05
    g31: Circle CenterX=-4.75 CenterY=-325.75 CenterZ=0 NormalX=0 NormalY=0 NormalZ=1 AngleXU=0 Radius=1.05
    g32: Circle CenterX=-4.75 CenterY=-63.15 CenterZ=0 NormalX=0 NormalY=0 NormalZ=1 AngleXU=0 Radius=1.05
    g33: Circle CenterX=-4.75 CenterY=-73.25 CenterZ=0 NormalX=0 NormalY=0 NormalZ=1 AngleXU=0 Radius=1.05
    g34: Circle CenterX=-4.75 CenterY=-83.35 CenterZ=0 NormalX=0 NormalY=0 NormalZ=1 AngleXU=0 Radius=1.05
    g35: Circle CenterX=-4.75 CenterY=-93.45 CenterZ=0 NormalX=0 NormalY=0 NormalZ=1 AngleXU=0 Radius=1.05
    g36: Circle CenterX=-4.75 CenterY=-103.55 CenterZ=0 NormalX=0 NormalY=0 NormalZ=1 AngleXU=0 Radius=1.05
    g37: Circle CenterX=-4.75 CenterY=-113.65 CenterZ=0 NormalX=0 NormalY=0 NormalZ=1 AngleXU=0 Radius=1.05
    g38: Circle CenterX=-4.75 CenterY=-123.75 CenterZ=0 NormalX=0 NormalY=0 NormalZ=1 AngleXU=0 Radius=1.05
    g39: Circle CenterX=-4.75 CenterY=-133.85 CenterZ=0 NormalX=0 NormalY=0 NormalZ=1 AngleXU=0 Radius=1.05
    g40: Circle CenterX=-4.75 CenterY=-143.95 CenterZ=0 NormalX=0 NormalY=0 NormalZ=1 AngleXU=0 Radius=1.05
    g41: Circle CenterX=-4.75 CenterY=-154.05 CenterZ=0 NormalX=0 NormalY=0 NormalZ=1 AngleXU=0 Radius=1.05
    g42: Circle CenterX=-4.75 CenterY=-164.15 CenterZ=0 NormalX=0 NormalY=0 NormalZ=1 AngleXU=0 Radius=1.05
    g43: Circle CenterX=-4.75 CenterY=-12.65 CenterZ=0 NormalX=0 NormalY=0 NormalZ=1 AngleXU=0 Radius=1.05
    g44: Circle CenterX=-4.75 CenterY=-22.75 CenterZ=0 NormalX=0 NormalY=0 NormalZ=1 AngleXU=0 Radius=1.05
    g45: Circle CenterX=-4.75 CenterY=-32.85 CenterZ=0 NormalX=0 NormalY=0 NormalZ=1 AngleXU=0 Radius=1.05
    g46: Circle CenterX=-4.75 CenterY=-42.95 CenterZ=0 NormalX=0 NormalY=0 NormalZ=1 AngleXU=0 Radius=1.05
    g47: Circle CenterX=-4.75 CenterY=-53.05 CenterZ=0 NormalX=0 NormalY=0 NormalZ=1 AngleXU=0 Radius=1.05
  constraints (144):
    c: Diameter(g0) = 2.1
    c: Equal(g0,g1) = 2.1
    c: DistanceY(g0,g1) = 10.1
    c: Equal(g0,g3) = 2.1
    c: Equal(g3,g2) = 2.1
    c: DistanceY(g3,g2) = 10.1
    c: Equal(g0,g7) = 2.1
    c: Equal(g7,g6) = 2.1
    c: DistanceY(g7,g6) = 10.1
    c: Equal(g7,g5) = 2.1
    c: Equal(g5,g4) = 2.1
    c: DistanceY(g5,g4) = 10.1
    c: Equal(g0,g15) = 2.1
    c: Equal(g15,g14) = 2.1
    c: DistanceY(g15,g14) = 10.1
    c: Equal(g15,g13) = 2.1
    c: Equal(g13,g12) = 2.1
    c: DistanceY(g13,g12) = 10.1
    c: Equal(g15,g11) = 2.1
    c: Equal(g11,g10) = 2.1
    c: DistanceY(g11,g10) = 10.1
    c: Equal(g11,g9) = 2.1
    c: Equal(g9,g8) = 2.1
    c: DistanceY(g9,g8) = 10.1
    c: Equal(g0,g31) = 2.1
    c: Equal(g31,g30) = 2.1
    c: DistanceY(g31,g30) = 10.1
    c: Equal(g31,g29) = 2.1
    c: Equal(g29,g28) = 2.1
    c: DistanceY(g29,g28) = 10.1
    c: Equal(g31,g27) = 2.1
    c: Equal(g27,g26) = 2.1
    c: DistanceY(g27,g26) = 10.1
    c: Equal(g27,g25) = 2.1
    c: Equal(g25,g24) = 2.1
    c: DistanceY(g25,g24) = 10.1
    c: Equal(g31,g23) = 2.1
    c: Equal(g23,g22) = 2.1
    c: DistanceY(g23,g22) = 10.1
    c: Equal(g23,g21) = 2.1
    c: Equal(g21,g20) = 2.1
    c: DistanceY(g21,g20) = 10.1
    c: Equal(g23,g19) = 2.1
    c: Equal(g19,g18) = 2.1
    c: DistanceY(g19,g18) = 10.1
    c: Equal(g19,g17) = 2.1
    c: Equal(g17,g16) = 2.1
    c: DistanceY(g17,g16) = 10.1
    c: Equal(g42,g41) = 2.1
    c: DistanceY(g42,g41) = 10.1
    c: Equal(g42,g40) = 2.1
    c: Equal(g40,g39) = 2.1
    c: DistanceY(g40,g39) = 10.1
    c: Equal(g38,g37) = 2.1
    c: DistanceY(g38,g37) = 10.1
    c: Equal(g38,g36) = 2.1
    c: Equal(g36,g35) = 2.1
    c: DistanceY(g36,g35) = 10.1
    c: Equal(g38,g34) = 2.1
    c: Equal(g34,g33) = 2.1
    c: DistanceY(g34,g33) = 10.1
    c: Equal(g34,g32) = 2.1
    c: Equal(g47,g46) = 2.1
    c: DistanceY(g47,g46) = 10.1
    c: Equal(g45,g44) = 2.1
    c: DistanceY(g45,g44) = 10.1
    c: Equal(g45,g43) = 2.1
    c: DistanceY(g1,g3) = 10.1
    c: DistanceY(g2,g7) = 10.1
    c: DistanceY(g6,g5) = 10.1
    c: DistanceY(g4,g15) = 10.1
    c: DistanceY(g14,g13) = 10.1
    c: DistanceY(g8,g31) = 10.1
    c: DistanceY(g30,g29) = 10.1
    c: DistanceY(g28,g27) = 10.1
    c: DistanceY(g26,g25) = 10.1
    c: DistanceY(g24,g23) = 10.1
    c: DistanceY(g22,g21) = 10.1
    c: DistanceY(g20,g19) = 10.1
    c: DistanceY(g18,g17) = 10.1
    c: DistanceY(g16,g42) = 10.1
    c: DistanceY(g39,g38) = 10.1
    c: DistanceY(g37,g36) = 10.1
    c: DistanceY(g35,g34) = 10.1
    c: DistanceY(g33,g32) = 10.1
    c: DistanceY(g46,g45) = 10.1
    c: DistanceY(g32,g47) = 10.1
    c: DistanceY(g44,g43) = 10.1
    c: DistanceY(g12,g11) = 10.1
    c: DistanceY(g10,g9) = 10.1
    c: DistanceY(g41,g40) = 10.1
    c: DistanceY(g43,g-1) = 12.65
    c: DistanceX(g43,g-1) = 4.75
    c: DistanceX(g44,g-1) = 4.75
    c: DistanceX(g45,g-1) = 4.75
    c: DistanceX(g47,g-1) = 4.75
    c: DistanceX(g32,g-1) = 4.75
    c: DistanceX(g34,g-1) = 4.75
    c: DistanceX(g35,g-1) = 4.75
    c: DistanceX(g0,g-1) = 4.75
    c: DistanceX(g1,g-1) = 4.75
    c: DistanceX(g3,g-1) = 4.75
    c: DistanceX(g2,g-1) = 4.75
    c: DistanceX(g7,g-1) = 4.75
    c: DistanceX(g6,g-1) = 4.75
    c: DistanceX(g5,g-1) = 4.75
    c: DistanceX(g4,g-1) = 4.75
    c: DistanceX(g15,g-1) = 4.75
    c: DistanceX(g14,g-1) = 4.75
    c: DistanceX(g13,g-1) = 4.75
    c: DistanceX(g12,g-1) = 4.75
    c: DistanceX(g11,g-1) = 4.75
    c: DistanceX(g10,g-1) = 4.75
    c: DistanceX(g9,g-1) = 4.75
    c: DistanceX(g8,g-1) = 4.75
    c: DistanceX(g31,g-1) = 4.75
    c: DistanceX(g30,g-1) = 4.75
    c: DistanceX(g29,g-1) = 4.75
    c: DistanceX(g28,g-1) = 4.75
    c: DistanceX(g27,g-1) = 4.75
    c: DistanceX(g26,g-1) = 4.75
    c: DistanceX(g25,g-1) = 4.75
    c: DistanceX(g24,g-1) = 4.75
    c: DistanceX(g23,g-1) = 4.75
    c: DistanceX(g22,g-1) = 4.75
    c: DistanceX(g21,g-1) = 4.75
    c: DistanceX(g20,g-1) = 4.75
    c: DistanceX(g19,g-1) = 4.75
    c: DistanceX(g18,g-1) = 4.75
    c: DistanceX(g17,g-1) = 4.75
    c: DistanceX(g16,g-1) = 4.75
    c: DistanceX(g42,g-1) = 4.75
    c: DistanceX(g41,g-1) = 4.75
    c: DistanceX(g40,g-1) = 4.75
    c: DistanceX(g39,g-1) = 4.75
    c: DistanceX(g38,g-1) = 4.75
    c: DistanceX(g37,g-1) = 4.75
    c: DistanceX(g36,g-1) = 4.75
    c: DistanceX(g33,g-1) = 4.75
    c: DistanceX(g46,g-1) = 4.75
    c: Diameter(g43) = 2.1
    c: Diameter(g46) = 2.1
    c: Diameter(g32) = 2.1
    c: Diameter(g39) = 2.1
FEATURE [PartDesign::Body] Body056  label="Corps001"
  Group = -> [Sketch063]
  Origin = -> Origin056
  Placement = pos=(504.546,-15.4212,0) rot=(0,0,1;4.71239rad)
FEATURE [Sketcher::SketchObject] Sketch064
  FullyConstrained = false
  MapMode = 5
  Placement = pos=(0,0.3,0) rot=(1,0,0;1.5708rad)
  sketch-geometry (8):
    g0: LineSegment StartX=0.6 StartY=9 StartZ=0 EndX=0.6 EndY=0 EndZ=0
    g1: LineSegment StartX=0.1 StartY=0 StartZ=0 EndX=0.1 EndY=8.9 EndZ=0
    g2: LineSegment StartX=0.1 StartY=8.9 StartZ=0 EndX=0.5 EndY=8.9 EndZ=0
    g3: LineSegment StartX=0.5 StartY=8.9 StartZ=0 EndX=0.5 EndY=0 EndZ=0
    g4: LineSegment StartX=0.6 StartY=0 StartZ=0 EndX=0.5 EndY=0 EndZ=0
    g5: LineSegment StartX=0 StartY=9 StartZ=0 EndX=0.6 EndY=9 EndZ=0
    g6: LineSegment StartX=0.1 StartY=0 StartZ=0 EndX=0 EndY=0 EndZ=0
    g7: LineSegment StartX=0 StartY=0 StartZ=0 EndX=0 EndY=9 EndZ=0
  constraints (21):
    c: Vertical(g0)
    c: DistanceY(g0,g0) = 9
    c: PointOnObject(g1,g-1)
    c: Vertical(g1)
    c: Coincident(g2,g1)
    c: Horizontal(g2)
    c: Coincident(g3,g2)
    c: Vertical(g3)
    c: DistanceX(g2,g2) = 0.4
    c: DistanceX(g-1,g1) = 0.1
    c: DistanceY(g1,g1) = 8.9
    c: Coincident(g4,g0)
    c: Coincident(g4,g3)
    c: Horizontal(g4)
    c: Coincident(g5,g0)
    c: Horizontal(g5)
    c: Coincident(g6,g1)
    c: Coincident(g6,g-1)
    c: Coincident(g7,g6)
    c: Coincident(g7,g5)
    c: Vertical(g7)
FEATURE [PartDesign::Pad] Pad053
  Direction = (0,-1,2e-16)
  Length = 500
  Length2 = 10
  Placement = pos=(0,0.3,0) rot=(1,0,0;1.5708rad)
  Profile = -> Sketch064
  ReferenceAxis = -> Sketch064 [N_Axis]
  Type = 0
FEATURE [Sketcher::SketchObject] Sketch065
  FullyConstrained = false
  MapMode = 5
  Placement = pos=(0,0,0) rot=(0.57735,0.57735,0.57735;2.0944rad)
  sketch-geometry (6):
    g0: LineSegment StartX=-499.7 StartY=9.2 StartZ=0 EndX=-499.7 EndY=-0.3 EndZ=0
    g1: LineSegment StartX=-499.7 StartY=-0.3 StartZ=0 EndX=-490.2 EndY=-0.3 EndZ=0
    g2: LineSegment StartX=-490.2 StartY=-0.3 StartZ=0 EndX=-499.7 EndY=9.2 EndZ=0
    g3: LineSegment StartX=0.3 StartY=-0.3 StartZ=0 EndX=-9.2 EndY=-0.3 EndZ=0
    g4: LineSegment StartX=0.3 StartY=-0.3 StartZ=0 EndX=0.3 EndY=9.2 EndZ=0
    g5: LineSegment StartX=0.3 StartY=9.2 StartZ=0 EndX=-9.2 EndY=-0.3 EndZ=0
  constraints (12):
    c: Vertical(g0)
    c: Horizontal(g1)
    c: Coincident(g2,g1)
    c: Coincident(g2,g0)
    c: DistanceY(g0,g0) = 9.5
    c: DistanceX(g1,g1) = 9.5
    c: Coincident(g4,g3)
    c: Vertical(g4)
    c: Coincident(g5,g3)
    c: Angle(g4,g3) = 1.5708
    c: DistanceY(g4,g4) = 9.5
    c: DistanceX(g3,g3) = 9.5
FEATURE [PartDesign::Pocket] Pocket006
  BaseFeature = -> Pad053
  Direction = (-1,-1e-16,1e-16)
  Length = 5
  Length2 = 5
  Placement = pos=(0,0.3,0) rot=(1,0,0;1.5708rad)
  Profile = -> Sketch065
  ReferenceAxis = -> Sketch065 [N_Axis]
  Reversed = true
  Type = 1
FEATURE [Sketcher::SketchObject] Sketch066
  FullyConstrained = true
  MapMode = 5
  Placement = pos=(0,0.3,-0.3) rot=(0,1,0;1.5708rad)
  sketch-geometry (48):
    g0: Circle CenterX=-4.75 CenterY=-487.35 CenterZ=0 NormalX=0 NormalY=0 NormalZ=1 AngleXU=0 Radius=1.05
    g1: Circle CenterX=-4.75 CenterY=-477.25 CenterZ=0 NormalX=0 NormalY=0 NormalZ=1 AngleXU=0 Radius=1.05
    g2: Circle CenterX=-4.75 CenterY=-457.05 CenterZ=0 NormalX=0 NormalY=0 NormalZ=1 AngleXU=0 Radius=1.05
    g3: Circle CenterX=-4.75 CenterY=-467.15 CenterZ=0 NormalX=0 NormalY=0 NormalZ=1 AngleXU=0 Radius=1.05
    g4: Circle CenterX=-4.75 CenterY=-416.65 CenterZ=0 NormalX=0 NormalY=0 NormalZ=1 AngleXU=0 Radius=1.05
    g5: Circle CenterX=-4.75 CenterY=-426.75 CenterZ=0 NormalX=0 NormalY=0 NormalZ=1 AngleXU=0 Radius=1.05
    g6: Circle CenterX=-4.75 CenterY=-436.85 CenterZ=0 NormalX=0 NormalY=0 NormalZ=1 AngleXU=0 Radius=1.05
    g7: Circle CenterX=-4.75 CenterY=-446.95 CenterZ=0 NormalX=0 NormalY=0 NormalZ=1 AngleXU=0 Radius=1.05
    g8: Circle CenterX=-4.75 CenterY=-335.85 CenterZ=0 NormalX=0 NormalY=0 NormalZ=1 AngleXU=0 Radius=1.05
    g9: Circle CenterX=-4.75 CenterY=-345.95 CenterZ=0 NormalX=0 NormalY=0 NormalZ=1 AngleXU=0 Radius=1.05
    g10: Circle CenterX=-4.75 CenterY=-356.05 CenterZ=0 NormalX=0 NormalY=0 NormalZ=1 AngleXU=0 Radius=1.05
    g11: Circle CenterX=-4.75 CenterY=-366.15 CenterZ=0 NormalX=0 NormalY=0 NormalZ=1 AngleXU=0 Radius=1.05
    g12: Circle CenterX=-4.75 CenterY=-376.25 CenterZ=0 NormalX=0 NormalY=0 NormalZ=1 AngleXU=0 Radius=1.05
    g13: Circle CenterX=-4.75 CenterY=-386.35 CenterZ=0 NormalX=0 NormalY=0 NormalZ=1 AngleXU=0 Radius=1.05
    g14: Circle CenterX=-4.75 CenterY=-396.45 CenterZ=0 NormalX=0 NormalY=0 NormalZ=1 AngleXU=0 Radius=1.05
    g15: Circle CenterX=-4.75 CenterY=-406.55 CenterZ=0 NormalX=0 NormalY=0 NormalZ=1 AngleXU=0 Radius=1.05
    g16: Circle CenterX=-4.75 CenterY=-174.25 CenterZ=0 NormalX=0 NormalY=0 NormalZ=1 AngleXU=0 Radius=1.05
    g17: Circle CenterX=-4.75 CenterY=-184.35 CenterZ=0 NormalX=0 NormalY=0 NormalZ=1 AngleXU=0 Radius=1.05
    g18: Circle CenterX=-4.75 CenterY=-194.45 CenterZ=0 NormalX=0 NormalY=0 NormalZ=1 AngleXU=0 Radius=1.05
    g19: Circle CenterX=-4.75 CenterY=-204.55 CenterZ=0 NormalX=0 NormalY=0 NormalZ=1 AngleXU=0 Radius=1.05
    g20: Circle CenterX=-4.75 CenterY=-214.65 CenterZ=0 NormalX=0 NormalY=0 NormalZ=1 AngleXU=0 Radius=1.05
    g21: Circle CenterX=-4.75 CenterY=-224.75 CenterZ=0 NormalX=0 NormalY=0 NormalZ=1 AngleXU=0 Radius=1.05
    g22: Circle CenterX=-4.75 CenterY=-234.85 CenterZ=0 NormalX=0 NormalY=0 NormalZ=1 AngleXU=0 Radius=1.05
    g23: Circle CenterX=-4.75 CenterY=-244.95 CenterZ=0 NormalX=0 NormalY=0 NormalZ=1 AngleXU=0 Radius=1.05
    g24: Circle CenterX=-4.75 CenterY=-255.05 CenterZ=0 NormalX=0 NormalY=0 NormalZ=1 AngleXU=0 Radius=1.05
    g25: Circle CenterX=-4.75 CenterY=-265.15 CenterZ=0 NormalX=0 NormalY=0 NormalZ=1 AngleXU=0 Radius=1.05
    g26: Circle CenterX=-4.75 CenterY=-275.25 CenterZ=0 NormalX=0 NormalY=0 NormalZ=1 AngleXU=0 Radius=1.05
    g27: Circle CenterX=-4.75 CenterY=-285.35 CenterZ=0 NormalX=0 NormalY=0 NormalZ=1 AngleXU=0 Radius=1.05
    g28: Circle CenterX=-4.75 CenterY=-295.45 CenterZ=0 NormalX=0 NormalY=0 NormalZ=1 AngleXU=0 Radius=1.05
    g29: Circle CenterX=-4.75 CenterY=-305.55 CenterZ=0 NormalX=0 NormalY=0 NormalZ=1 AngleXU=0 Radius=1.05
    g30: Circle CenterX=-4.75 CenterY=-315.65 CenterZ=0 NormalX=0 NormalY=0 NormalZ=1 AngleXU=0 Radius=1.05
    g31: Circle CenterX=-4.75 CenterY=-325.75 CenterZ=0 NormalX=0 NormalY=0 NormalZ=1 AngleXU=0 Radius=1.05
    g32: Circle CenterX=-4.75 CenterY=-63.15 CenterZ=0 NormalX=0 NormalY=0 NormalZ=1 AngleXU=0 Radius=1.05
    g33: Circle CenterX=-4.75 CenterY=-73.25 CenterZ=0 NormalX=0 NormalY=0 NormalZ=1 AngleXU=0 Radius=1.05
    g34: Circle CenterX=-4.75 CenterY=-83.35 CenterZ=0 NormalX=0 NormalY=0 NormalZ=1 AngleXU=0 Radius=1.05
    g35: Circle CenterX=-4.75 CenterY=-93.45 CenterZ=0 NormalX=0 NormalY=0 NormalZ=1 AngleXU=0 Radius=1.05
    g36: Circle CenterX=-4.75 CenterY=-103.55 CenterZ=0 NormalX=0 NormalY=0 NormalZ=1 AngleXU=0 Radius=1.05
    g37: Circle CenterX=-4.75 CenterY=-113.65 CenterZ=0 NormalX=0 NormalY=0 NormalZ=1 AngleXU=0 Radius=1.05
    g38: Circle CenterX=-4.75 CenterY=-123.75 CenterZ=0 NormalX=0 NormalY=0 NormalZ=1 AngleXU=0 Radius=1.05
    g39: Circle CenterX=-4.75 CenterY=-133.85 CenterZ=0 NormalX=0 NormalY=0 NormalZ=1 AngleXU=0 Radius=1.05
    g40: Circle CenterX=-4.75 CenterY=-143.95 CenterZ=0 NormalX=0 NormalY=0 NormalZ=1 AngleXU=0 Radius=1.05
    g41: Circle CenterX=-4.75 CenterY=-154.05 CenterZ=0 NormalX=0 NormalY=0 NormalZ=1 AngleXU=0 Radius=1.05
    g42: Circle CenterX=-4.75 CenterY=-164.15 CenterZ=0 NormalX=0 NormalY=0 NormalZ=1 AngleXU=0 Radius=1.05
    g43: Circle CenterX=-4.75 CenterY=-12.65 CenterZ=0 NormalX=0 NormalY=0 NormalZ=1 AngleXU=0 Radius=1.05
    g44: Circle CenterX=-4.75 CenterY=-22.75 CenterZ=0 NormalX=0 NormalY=0 NormalZ=1 AngleXU=0 Radius=1.05
    g45: Circle CenterX=-4.75 CenterY=-32.85 CenterZ=0 NormalX=0 NormalY=0 NormalZ=1 AngleXU=0 Radius=1.05
    g46: Circle CenterX=-4.75 CenterY=-42.95 CenterZ=0 NormalX=0 NormalY=0 NormalZ=1 AngleXU=0 Radius=1.05
    g47: Circle CenterX=-4.75 CenterY=-53.05 CenterZ=0 NormalX=0 NormalY=0 NormalZ=1 AngleXU=0 Radius=1.05
  constraints (144):
    c: Diameter(g0) = 2.1
    c: Equal(g0,g1) = 2.1
    c: DistanceY(g0,g1) = 10.1
    c: Equal(g0,g3) = 2.1
    c: Equal(g3,g2) = 2.1
    c: DistanceY(g3,g2) = 10.1
    c: Equal(g0,g7) = 2.1
    c: Equal(g7,g6) = 2.1
    c: DistanceY(g7,g6) = 10.1
    c: Equal(g7,g5) = 2.1
    c: Equal(g5,g4) = 2.1
    c: DistanceY(g5,g4) = 10.1
    c: Equal(g0,g15) = 2.1
    c: Equal(g15,g14) = 2.1
    c: DistanceY(g15,g14) = 10.1
    c: Equal(g15,g13) = 2.1
    c: Equal(g13,g12) = 2.1
    c: DistanceY(g13,g12) = 10.1
    c: Equal(g15,g11) = 2.1
    c: Equal(g11,g10) = 2.1
    c: DistanceY(g11,g10) = 10.1
    c: Equal(g11,g9) = 2.1
    c: Equal(g9,g8) = 2.1
    c: DistanceY(g9,g8) = 10.1
    c: Equal(g0,g31) = 2.1
    c: Equal(g31,g30) = 2.1
    c: DistanceY(g31,g30) = 10.1
    c: Equal(g31,g29) = 2.1
    c: Equal(g29,g28) = 2.1
    c: DistanceY(g29,g28) = 10.1
    c: Equal(g31,g27) = 2.1
    c: Equal(g27,g26) = 2.1
    c: DistanceY(g27,g26) = 10.1
    c: Equal(g27,g25) = 2.1
    c: Equal(g25,g24) = 2.1
    c: DistanceY(g25,g24) = 10.1
    c: Equal(g31,g23) = 2.1
    c: Equal(g23,g22) = 2.1
    c: DistanceY(g23,g22) = 10.1
    c: Equal(g23,g21) = 2.1
    c: Equal(g21,g20) = 2.1
    c: DistanceY(g21,g20) = 10.1
    c: Equal(g23,g19) = 2.1
    c: Equal(g19,g18) = 2.1
    c: DistanceY(g19,g18) = 10.1
    c: Equal(g19,g17) = 2.1
    c: Equal(g17,g16) = 2.1
    c: DistanceY(g17,g16) = 10.1
    c: Equal(g42,g41) = 2.1
    c: DistanceY(g42,g41) = 10.1
    c: Equal(g42,g40) = 2.1
    c: Equal(g40,g39) = 2.1
    c: DistanceY(g40,g39) = 10.1
    c: Equal(g38,g37) = 2.1
    c: DistanceY(g38,g37) = 10.1
    c: Equal(g38,g36) = 2.1
    c: Equal(g36,g35) = 2.1
    c: DistanceY(g36,g35) = 10.1
    c: Equal(g38,g34) = 2.1
    c: Equal(g34,g33) = 2.1
    c: DistanceY(g34,g33) = 10.1
    c: Equal(g34,g32) = 2.1
    c: Equal(g47,g46) = 2.1
    c: DistanceY(g47,g46) = 10.1
    c: Equal(g45,g44) = 2.1
    c: DistanceY(g45,g44) = 10.1
    c: Equal(g45,g43) = 2.1
    c: DistanceY(g1,g3) = 10.1
    c: DistanceY(g2,g7) = 10.1
    c: DistanceY(g6,g5) = 10.1
    c: DistanceY(g4,g15) = 10.1
    c: DistanceY(g14,g13) = 10.1
    c: DistanceY(g8,g31) = 10.1
    c: DistanceY(g30,g29) = 10.1
    c: DistanceY(g28,g27) = 10.1
    c: DistanceY(g26,g25) = 10.1
    c: DistanceY(g24,g23) = 10.1
    c: DistanceY(g22,g21) = 10.1
    c: DistanceY(g20,g19) = 10.1
    c: DistanceY(g18,g17) = 10.1
    c: DistanceY(g16,g42) = 10.1
    c: DistanceY(g39,g38) = 10.1
    c: DistanceY(g37,g36) = 10.1
    c: DistanceY(g35,g34) = 10.1
    c: DistanceY(g33,g32) = 10.1
    c: DistanceY(g46,g45) = 10.1
    c: DistanceY(g32,g47) = 10.1
    c: DistanceY(g44,g43) = 10.1
    c: DistanceY(g12,g11) = 10.1
    c: DistanceY(g10,g9) = 10.1
    c: DistanceY(g41,g40) = 10.1
    c: DistanceY(g43,g-1) = 12.65
    c: DistanceX(g43,g-1) = 4.75
    c: DistanceX(g44,g-1) = 4.75
    c: DistanceX(g45,g-1) = 4.75
    c: DistanceX(g47,g-1) = 4.75
    c: DistanceX(g32,g-1) = 4.75
    c: DistanceX(g34,g-1) = 4.75
    c: DistanceX(g35,g-1) = 4.75
    c: DistanceX(g0,g-1) = 4.75
    c: DistanceX(g1,g-1) = 4.75
    c: DistanceX(g3,g-1) = 4.75
    c: DistanceX(g2,g-1) = 4.75
    c: DistanceX(g7,g-1) = 4.75
    c: DistanceX(g6,g-1) = 4.75
    c: DistanceX(g5,g-1) = 4.75
    c: DistanceX(g4,g-1) = 4.75
    c: DistanceX(g15,g-1) = 4.75
    c: DistanceX(g14,g-1) = 4.75
    c: DistanceX(g13,g-1) = 4.75
    c: DistanceX(g12,g-1) = 4.75
    c: DistanceX(g11,g-1) = 4.75
    c: DistanceX(g10,g-1) = 4.75
    c: DistanceX(g9,g-1) = 4.75
    c: DistanceX(g8,g-1) = 4.75
    c: DistanceX(g31,g-1) = 4.75
    c: DistanceX(g30,g-1) = 4.75
    c: DistanceX(g29,g-1) = 4.75
    c: DistanceX(g28,g-1) = 4.75
    c: DistanceX(g27,g-1) = 4.75
    c: DistanceX(g26,g-1) = 4.75
    c: DistanceX(g25,g-1) = 4.75
    c: DistanceX(g24,g-1) = 4.75
    c: DistanceX(g23,g-1) = 4.75
    c: DistanceX(g22,g-1) = 4.75
    c: DistanceX(g21,g-1) = 4.75
    c: DistanceX(g20,g-1) = 4.75
    c: DistanceX(g19,g-1) = 4.75
    c: DistanceX(g18,g-1) = 4.75
    c: DistanceX(g17,g-1) = 4.75
    c: DistanceX(g16,g-1) = 4.75
    c: DistanceX(g42,g-1) = 4.75
    c: DistanceX(g41,g-1) = 4.75
    c: DistanceX(g40,g-1) = 4.75
    c: DistanceX(g39,g-1) = 4.75
    c: DistanceX(g38,g-1) = 4.75
    c: DistanceX(g37,g-1) = 4.75
    c: DistanceX(g36,g-1) = 4.75
    c: DistanceX(g33,g-1) = 4.75
    c: DistanceX(g46,g-1) = 4.75
    c: Diameter(g43) = 2.1
    c: Diameter(g46) = 2.1
    c: Diameter(g32) = 2.1
    c: Diameter(g39) = 2.1
FEATURE [PartDesign::Pocket] Pocket007
  BaseFeature = -> Pocket006
  Direction = (-1,0,-2e-16)
  Length = 10
  Length2 = 5
  Placement = pos=(0,0.3,0) rot=(1,0,0;1.5708rad)
  Profile = -> Sketch066
  ReferenceAxis = -> Sketch066 [N_Axis]
  Refine = true
  Reversed = true
  Type = 1
FEATURE [PartDesign::Body] Body054  label="join caoutchou001"
  Group = -> [Sketch064,Pad053,Sketch065,Pocket006,Sketch066,Pocket007]
  Origin = -> Origin054
  Placement = pos=(504.246,-15.1212,0.2) rot=(0.57735,0.57735,0.57735;4.18879rad)
  Tip = -> Pocket007
FEATURE [Sketcher::SketchObject] Sketch067
  FullyConstrained = true
  MapMode = 5
  sketch-geometry (1):
    g0: Circle CenterX=-4.75 CenterY=-22.75 CenterZ=0 NormalX=0 NormalY=0 NormalZ=1 AngleXU=0 Radius=1.05
  constraints (3):
    c: Diameter(g0) = 2.1
    c: Distance(g0,g-2) = 4.75
    c: Distance(g0,g-1) = 22.75
FEATURE [PartDesign::Pad] Pad054
  Direction = (0,0,1)
  Length = 0.6
  Length2 = 10
  Profile = -> Sketch067
  ReferenceAxis = -> Sketch067 [N_Axis]
  Refine = true
  Type = 0
FEATURE [PartDesign::Body] Body057  label="entretoises049"
  Group = -> [Sketch067,Pad054]
  Origin = -> Origin057
  Placement = pos=(504.546,-15.4212,0) rot=(0,0,-1;1.5708rad)
  Tip = -> Pad054
FEATURE [Sketcher::SketchObject] Sketch068
  FullyConstrained = true
  MapMode = 5
  Placement = pos=(0,0,0.2) rot=(0,0,1;0rad)
  sketch-geometry (1):
    g0: Circle CenterX=-4.75 CenterY=-12.65 CenterZ=0 NormalX=0 NormalY=0 NormalZ=1 AngleXU=0 Radius=1.05
  constraints (3):
    c: Diameter(g0) = 2.1
    c: Distance(g0,g-2) = 4.75
    c: Distance(g0,g-1) = 12.65
FEATURE [PartDesign::Pad] Pad055
  Direction = (0,0,1)
  Length = 0.6
  Length2 = 10
  Placement = pos=(0,0,0.2) rot=(0,0,1;0rad)
  Profile = -> Sketch068
  ReferenceAxis = -> Sketch068 [N_Axis]
  Refine = true
  Type = 0
FEATURE [PartDesign::Body] Body058  label="entretoises050"
  Group = -> [Sketch068,Pad055]
  Origin = -> Origin058
  Placement = pos=(504.546,-15.4212,0) rot=(0,0,-1;1.5708rad)
  Tip = -> Pad055
FEATURE [Sketcher::SketchObject] Sketch069
  FullyConstrained = true
  MapMode = 5
  Placement = pos=(0,0,0.2) rot=(0,0,1;0rad)
  sketch-geometry (1):
    g0: Circle CenterX=-4.75 CenterY=-32.85 CenterZ=0 NormalX=0 NormalY=0 NormalZ=1 AngleXU=0 Radius=1.05
  constraints (3):
    c: Diameter(g0) = 2.1
    c: Distance(g0,g-2) = 4.75
    c: Distance(g0,g-1) = 32.85
FEATURE [PartDesign::Pad] Pad056
  Direction = (0,0,1)
  Length = 0.6
  Length2 = 10
  Placement = pos=(0,0,0.2) rot=(0,0,1;0rad)
  Profile = -> Sketch069
  ReferenceAxis = -> Sketch069 [N_Axis]
  Refine = true
  Type = 0
FEATURE [PartDesign::Body] Body059  label="entretoises051"
  Group = -> [Sketch069,Pad056]
  Origin = -> Origin059
  Placement = pos=(504.546,-15.4212,0) rot=(0,0,-1;1.5708rad)
  Tip = -> Pad056
FEATURE [Sketcher::SketchObject] Sketch070
  FullyConstrained = true
  MapMode = 5
  Placement = pos=(0,0,0.2) rot=(0,0,1;0rad)
  sketch-geometry (1):
    g0: Circle CenterX=-4.75 CenterY=-42.95 CenterZ=0 NormalX=0 NormalY=0 NormalZ=1 AngleXU=0 Radius=1.05
  constraints (3):
    c: Diameter(g0) = 2.1
    c: Distance(g0,g-2) = 4.75
    c: Distance(g0,g-1) = 42.95
FEATURE [PartDesign::Pad] Pad057
  Direction = (0,0,1)
  Length = 0.6
  Length2 = 10
  Placement = pos=(0,0,0.2) rot=(0,0,1;0rad)
  Profile = -> Sketch070
  ReferenceAxis = -> Sketch070 [N_Axis]
  Refine = true
  Type = 0
FEATURE [PartDesign::Body] Body060  label="entretoises052"
  Group = -> [Sketch070,Pad057]
  Origin = -> Origin060
  Placement = pos=(504.546,-15.4212,0) rot=(0,0,-1;1.5708rad)
  Tip = -> Pad057
FEATURE [Sketcher::SketchObject] Sketch071
  FullyConstrained = true
  MapMode = 5
  Placement = pos=(0,0,0.2) rot=(0,0,1;0rad)
  sketch-geometry (1):
    g0: Circle CenterX=-4.75 CenterY=-53.05 CenterZ=0 NormalX=0 NormalY=0 NormalZ=1 AngleXU=0 Radius=1.05
  constraints (3):
    c: Diameter(g0) = 2.1
    c: Distance(g0,g-2) = 4.75
    c: Distance(g0,g-1) = 53.05
FEATURE [PartDesign::Pad] Pad058
  Direction = (0,0,1)
  Length = 0.6
  Length2 = 10
  Placement = pos=(0,0,0.2) rot=(0,0,1;0rad)
  Profile = -> Sketch071
  ReferenceAxis = -> Sketch071 [N_Axis]
  Refine = true
  Type = 0
FEATURE [PartDesign::Body] Body061  label="entretoises053"
  Group = -> [Sketch071,Pad058]
  Origin = -> Origin061
  Placement = pos=(504.546,-15.4212,0) rot=(0,0,-1;1.5708rad)
  Tip = -> Pad058
FEATURE [Sketcher::SketchObject] Sketch072
  FullyConstrained = true
  MapMode = 5
  Placement = pos=(0,0,0.2) rot=(0,0,1;0rad)
  sketch-geometry (1):
    g0: Circle CenterX=-4.75 CenterY=-22.75 CenterZ=0 NormalX=0 NormalY=0 NormalZ=1 AngleXU=0 Radius=1.05
  constraints (3):
    c: Diameter(g0) = 2.1
    c: Distance(g0,g-2) = 4.75
    c: Distance(g0,g-1) = 22.75
FEATURE [PartDesign::Pad] Pad059
  Direction = (0,0,1)
  Length = 0.6
  Length2 = 10
  Placement = pos=(0,0,0.2) rot=(0,0,1;0rad)
  Profile = -> Sketch072
  ReferenceAxis = -> Sketch072 [N_Axis]
  Refine = true
  Type = 0
FEATURE [PartDesign::Body] Body062  label="entretoises054"
  Group = -> [Sketch072,Pad059]
  Origin = -> Origin062
  Placement = pos=(504.546,-15.4212,0) rot=(0,0,-1;1.5708rad)
  Tip = -> Pad059
FEATURE [Sketcher::SketchObject] Sketch073
  FullyConstrained = true
  MapMode = 5
  Placement = pos=(0,0,0.2) rot=(0,0,1;0rad)
  sketch-geometry (1):
    g0: Circle CenterX=-4.75 CenterY=-63.15 CenterZ=0 NormalX=0 NormalY=0 NormalZ=1 AngleXU=0 Radius=1.05
  constraints (3):
    c: Diameter(g0) = 2.1
    c: Distance(g0,g-2) = 4.75
    c: Distance(g0,g-1) = 63.15
FEATURE [PartDesign::Pad] Pad060
  Direction = (0,0,1)
  Length = 0.6
  Length2 = 10
  Placement = pos=(0,0,0.2) rot=(0,0,1;0rad)
  Profile = -> Sketch073
  ReferenceAxis = -> Sketch073 [N_Axis]
  Refine = true
  Type = 0
FEATURE [PartDesign::Body] Body063  label="entretoises055"
  Group = -> [Sketch073,Pad060]
  Origin = -> Origin063
  Placement = pos=(504.546,-15.4212,0) rot=(0,0,-1;1.5708rad)
  Tip = -> Pad060
FEATURE [Sketcher::SketchObject] Sketch074
  FullyConstrained = true
  MapMode = 5
  Placement = pos=(0,0,0.2) rot=(0,0,1;0rad)
  sketch-geometry (1):
    g0: Circle CenterX=-4.75 CenterY=-73.25 CenterZ=0 NormalX=0 NormalY=0 NormalZ=1 AngleXU=0 Radius=1.05
  constraints (3):
    c: Diameter(g0) = 2.1
    c: Distance(g0,g-2) = 4.75
    c: Distance(g0,g-1) = 73.25
FEATURE [PartDesign::Pad] Pad061
  Direction = (0,0,1)
  Length = 0.6
  Length2 = 10
  Placement = pos=(0,0,0.2) rot=(0,0,1;0rad)
  Profile = -> Sketch074
  ReferenceAxis = -> Sketch074 [N_Axis]
  Refine = true
  Type = 0
FEATURE [PartDesign::Body] Body064  label="entretoises056"
  Group = -> [Sketch074,Pad061]
  Origin = -> Origin064
  Placement = pos=(504.546,-15.4212,0) rot=(0,0,-1;1.5708rad)
  Tip = -> Pad061
FEATURE [Sketcher::SketchObject] Sketch075
  FullyConstrained = true
  MapMode = 5
  Placement = pos=(0,0,0.2) rot=(0,0,1;0rad)
  sketch-geometry (1):
    g0: Circle CenterX=-4.75 CenterY=-83.35 CenterZ=0 NormalX=0 NormalY=0 NormalZ=1 AngleXU=0 Radius=1.05
  constraints (3):
    c: Diameter(g0) = 2.1
    c: Distance(g0,g-2) = 4.75
    c: Distance(g0,g-1) = 83.35
FEATURE [PartDesign::Pad] Pad062
  Direction = (0,0,1)
  Length = 0.6
  Length2 = 10
  Placement = pos=(0,0,0.2) rot=(0,0,1;0rad)
  Profile = -> Sketch075
  ReferenceAxis = -> Sketch075 [N_Axis]
  Refine = true
  Type = 0
FEATURE [PartDesign::Body] Body065  label="entretoises057"
  Group = -> [Sketch075,Pad062]
  Origin = -> Origin065
  Placement = pos=(504.546,-15.4212,0) rot=(0,0,-1;1.5708rad)
  Tip = -> Pad062
FEATURE [Sketcher::SketchObject] Sketch076
  FullyConstrained = true
  MapMode = 5
  Placement = pos=(0,0,0.2) rot=(0,0,1;0rad)
  sketch-geometry (1):
    g0: Circle CenterX=-4.75 CenterY=-93.45 CenterZ=0 NormalX=0 NormalY=0 NormalZ=1 AngleXU=0 Radius=1.05
  constraints (3):
    c: Diameter(g0) = 2.1
    c: Distance(g0,g-2) = 4.75
    c: Distance(g0,g-1) = 93.45
FEATURE [PartDesign::Pad] Pad063
  Direction = (0,0,1)
  Length = 0.6
  Length2 = 10
  Placement = pos=(0,0,0.2) rot=(0,0,1;0rad)
  Profile = -> Sketch076
  ReferenceAxis = -> Sketch076 [N_Axis]
  Refine = true
  Type = 0
FEATURE [PartDesign::Body] Body066  label="entretoises058"
  Group = -> [Sketch076,Pad063]
  Origin = -> Origin066
  Placement = pos=(504.546,-15.4212,0) rot=(0,0,-1;1.5708rad)
  Tip = -> Pad063
FEATURE [Sketcher::SketchObject] Sketch077
  FullyConstrained = true
  MapMode = 5
  Placement = pos=(0,0,0.2) rot=(0,0,1;0rad)
  sketch-geometry (1):
    g0: Circle CenterX=-4.75 CenterY=-103.55 CenterZ=0 NormalX=0 NormalY=0 NormalZ=1 AngleXU=0 Radius=1.05
  constraints (3):
    c: Diameter(g0) = 2.1
    c: Distance(g0,g-2) = 4.75
    c: Distance(g0,g-1) = 103.55
FEATURE [PartDesign::Pad] Pad064
  Direction = (0,0,1)
  Length = 0.6
  Length2 = 10
  Placement = pos=(0,0,0.2) rot=(0,0,1;0rad)
  Profile = -> Sketch077
  ReferenceAxis = -> Sketch077 [N_Axis]
  Refine = true
  Type = 0
FEATURE [PartDesign::Body] Body067  label="entretoises059"
  Group = -> [Sketch077,Pad064]
  Origin = -> Origin067
  Placement = pos=(504.546,-15.4212,0) rot=(0,0,-1;1.5708rad)
  Tip = -> Pad064
FEATURE [Sketcher::SketchObject] Sketch078
  FullyConstrained = true
  MapMode = 5
  Placement = pos=(0,0,0.2) rot=(0,0,1;0rad)
  sketch-geometry (1):
    g0: Circle CenterX=-4.75 CenterY=-113.65 CenterZ=0 NormalX=0 NormalY=0 NormalZ=1 AngleXU=0 Radius=1.05
  constraints (3):
    c: Diameter(g0) = 2.1
    c: Distance(g0,g-2) = 4.75
    c: Distance(g0,g-1) = 113.65
FEATURE [PartDesign::Pad] Pad065
  Direction = (0,0,1)
  Length = 0.6
  Length2 = 10
  Placement = pos=(0,0,0.2) rot=(0,0,1;0rad)
  Profile = -> Sketch078
  ReferenceAxis = -> Sketch078 [N_Axis]
  Refine = true
  Type = 0
FEATURE [PartDesign::Body] Body068  label="entretoises060"
  Group = -> [Sketch078,Pad065]
  Origin = -> Origin068
  Placement = pos=(504.546,-15.4212,0) rot=(0,0,-1;1.5708rad)
  Tip = -> Pad065
FEATURE [Sketcher::SketchObject] Sketch079
  FullyConstrained = true
  MapMode = 5
  Placement = pos=(0,0,0.2) rot=(0,0,1;0rad)
  sketch-geometry (1):
    g0: Circle CenterX=-4.75 CenterY=-123.75 CenterZ=0 NormalX=0 NormalY=0 NormalZ=1 AngleXU=0 Radius=1.05
  constraints (3):
    c: Diameter(g0) = 2.1
    c: Distance(g0,g-2) = 4.75
    c: Distance(g0,g-1) = 123.75
FEATURE [PartDesign::Pad] Pad066
  Direction = (0,0,1)
  Length = 0.6
  Length2 = 10
  Placement = pos=(0,0,0.2) rot=(0,0,1;0rad)
  Profile = -> Sketch079
  ReferenceAxis = -> Sketch079 [N_Axis]
  Refine = true
  Type = 0
FEATURE [PartDesign::Body] Body069  label="entretoises061"
  Group = -> [Sketch079,Pad066]
  Origin = -> Origin069
  Placement = pos=(504.546,-15.4212,0) rot=(0,0,-1;1.5708rad)
  Tip = -> Pad066
FEATURE [Sketcher::SketchObject] Sketch080
  FullyConstrained = true
  MapMode = 5
  Placement = pos=(0,0,0.2) rot=(0,0,1;0rad)
  sketch-geometry (1):
    g0: Circle CenterX=-4.75 CenterY=-133.85 CenterZ=0 NormalX=0 NormalY=0 NormalZ=1 AngleXU=0 Radius=1.05
  constraints (3):
    c: Diameter(g0) = 2.1
    c: Distance(g0,g-2) = 4.75
    c: Distance(g0,g-1) = 133.85
FEATURE [PartDesign::Pad] Pad067
  Direction = (0,0,1)
  Length = 0.6
  Length2 = 10
  Placement = pos=(0,0,0.2) rot=(0,0,1;0rad)
  Profile = -> Sketch080
  ReferenceAxis = -> Sketch080 [N_Axis]
  Refine = true
  Type = 0
FEATURE [PartDesign::Body] Body070  label="entretoises062"
  Group = -> [Sketch080,Pad067]
  Origin = -> Origin070
  Placement = pos=(504.546,-15.4212,0) rot=(0,0,-1;1.5708rad)
  Tip = -> Pad067
FEATURE [Sketcher::SketchObject] Sketch081
  FullyConstrained = true
  MapMode = 5
  Placement = pos=(0,0,0.2) rot=(0,0,1;0rad)
  sketch-geometry (1):
    g0: Circle CenterX=-4.75 CenterY=-143.95 CenterZ=0 NormalX=0 NormalY=0 NormalZ=1 AngleXU=0 Radius=1.05
  constraints (3):
    c: Diameter(g0) = 2.1
    c: Distance(g0,g-2) = 4.75
    c: Distance(g0,g-1) = 143.95
FEATURE [PartDesign::Pad] Pad068
  Direction = (0,0,1)
  Length = 0.6
  Length2 = 10
  Placement = pos=(0,0,0.2) rot=(0,0,1;0rad)
  Profile = -> Sketch081
  ReferenceAxis = -> Sketch081 [N_Axis]
  Refine = true
  Type = 0
FEATURE [PartDesign::Body] Body071  label="entretoises063"
  Group = -> [Sketch081,Pad068]
  Origin = -> Origin071
  Placement = pos=(504.546,-15.4212,0) rot=(0,0,-1;1.5708rad)
  Tip = -> Pad068
FEATURE [Sketcher::SketchObject] Sketch082
  FullyConstrained = true
  MapMode = 5
  Placement = pos=(0,0,0.2) rot=(0,0,1;0rad)
  sketch-geometry (1):
    g0: Circle CenterX=-4.75 CenterY=-154.05 CenterZ=0 NormalX=0 NormalY=0 NormalZ=1 AngleXU=0 Radius=1.05
  constraints (3):
    c: Diameter(g0) = 2.1
    c: Distance(g0,g-2) = 4.75
    c: Distance(g0,g-1) = 154.05
FEATURE [PartDesign::Pad] Pad069
  Direction = (0,0,1)
  Length = 0.6
  Length2 = 10
  Placement = pos=(0,0,0.2) rot=(0,0,1;0rad)
  Profile = -> Sketch082
  ReferenceAxis = -> Sketch082 [N_Axis]
  Refine = true
  Type = 0
FEATURE [PartDesign::Body] Body072  label="entretoises064"
  Group = -> [Sketch082,Pad069]
  Origin = -> Origin072
  Placement = pos=(504.546,-15.4212,0) rot=(0,0,-1;1.5708rad)
  Tip = -> Pad069
FEATURE [Sketcher::SketchObject] Sketch083
  FullyConstrained = true
  MapMode = 5
  Placement = pos=(0,0,0.2) rot=(0,0,1;0rad)
  sketch-geometry (1):
    g0: Circle CenterX=-4.75 CenterY=-164.15 CenterZ=0 NormalX=0 NormalY=0 NormalZ=1 AngleXU=0 Radius=1.05
  constraints (3):
    c: Diameter(g0) = 2.1
    c: Distance(g0,g-2) = 4.75
    c: Distance(g0,g-1) = 164.15
FEATURE [PartDesign::Pad] Pad070
  Direction = (0,0,1)
  Length = 0.6
  Length2 = 10
  Placement = pos=(0,0,0.2) rot=(0,0,1;0rad)
  Profile = -> Sketch083
  ReferenceAxis = -> Sketch083 [N_Axis]
  Refine = true
  Type = 0
FEATURE [PartDesign::Body] Body073  label="entretoises065"
  Group = -> [Sketch083,Pad070]
  Origin = -> Origin073
  Placement = pos=(504.546,-15.4212,0) rot=(0,0,-1;1.5708rad)
  Tip = -> Pad070
FEATURE [Sketcher::SketchObject] Sketch084
  FullyConstrained = true
  MapMode = 5
  Placement = pos=(0,0,0.2) rot=(0,0,1;0rad)
  sketch-geometry (1):
    g0: Circle CenterX=-4.75 CenterY=-174.25 CenterZ=0 NormalX=0 NormalY=0 NormalZ=1 AngleXU=0 Radius=1.05
  constraints (3):
    c: Diameter(g0) = 2.1
    c: Distance(g0,g-2) = 4.75
    c: Distance(g0,g-1) = 174.25
FEATURE [PartDesign::Pad] Pad071
  Direction = (0,0,1)
  Length = 0.6
  Length2 = 10
  Placement = pos=(0,0,0.2) rot=(0,0,1;0rad)
  Profile = -> Sketch084
  ReferenceAxis = -> Sketch084 [N_Axis]
  Refine = true
  Type = 0
FEATURE [PartDesign::Body] Body074  label="entretoises066"
  Group = -> [Sketch084,Pad071]
  Origin = -> Origin074
  Placement = pos=(504.546,-15.4212,0) rot=(0,0,-1;1.5708rad)
  Tip = -> Pad071
FEATURE [Sketcher::SketchObject] Sketch085
  FullyConstrained = true
  MapMode = 5
  Placement = pos=(0,0,0.2) rot=(0,0,1;0rad)
  sketch-geometry (1):
    g0: Circle CenterX=-4.75 CenterY=-184.35 CenterZ=0 NormalX=0 NormalY=0 NormalZ=1 AngleXU=0 Radius=1.05
  constraints (3):
    c: Diameter(g0) = 2.1
    c: Distance(g0,g-2) = 4.75
    c: Distance(g0,g-1) = 184.35
FEATURE [PartDesign::Pad] Pad072
  Direction = (0,0,1)
  Length = 0.6
  Length2 = 10
  Placement = pos=(0,0,0.2) rot=(0,0,1;0rad)
  Profile = -> Sketch085
  ReferenceAxis = -> Sketch085 [N_Axis]
  Refine = true
  Type = 0
FEATURE [PartDesign::Body] Body075  label="entretoises067"
  Group = -> [Sketch085,Pad072]
  Origin = -> Origin075
  Placement = pos=(504.546,-15.4212,0) rot=(0,0,-1;1.5708rad)
  Tip = -> Pad072
FEATURE [Sketcher::SketchObject] Sketch086
  FullyConstrained = true
  MapMode = 5
  Placement = pos=(0,0,0.2) rot=(0,0,1;0rad)
  sketch-geometry (1):
    g0: Circle CenterX=-4.75 CenterY=-194.45 CenterZ=0 NormalX=0 NormalY=0 NormalZ=1 AngleXU=0 Radius=1.05
  constraints (3):
    c: Diameter(g0) = 2.1
    c: Distance(g0,g-2) = 4.75
    c: Distance(g0,g-1) = 194.45
FEATURE [PartDesign::Pad] Pad073
  Direction = (0,0,1)
  Length = 0.6
  Length2 = 10
  Placement = pos=(0,0,0.2) rot=(0,0,1;0rad)
  Profile = -> Sketch086
  ReferenceAxis = -> Sketch086 [N_Axis]
  Refine = true
  Type = 0
FEATURE [PartDesign::Body] Body076  label="entretoises068"
  Group = -> [Sketch086,Pad073]
  Origin = -> Origin076
  Placement = pos=(504.546,-15.4212,0) rot=(0,0,-1;1.5708rad)
  Tip = -> Pad073
FEATURE [Sketcher::SketchObject] Sketch087
  FullyConstrained = true
  MapMode = 5
  Placement = pos=(0,0,0.2) rot=(0,0,1;0rad)
  sketch-geometry (1):
    g0: Circle CenterX=-4.75 CenterY=-204.55 CenterZ=0 NormalX=0 NormalY=0 NormalZ=1 AngleXU=0 Radius=1.05
  constraints (3):
    c: Diameter(g0) = 2.1
    c: Distance(g0,g-2) = 4.75
    c: Distance(g0,g-1) = 204.55
FEATURE [PartDesign::Pad] Pad074
  Direction = (0,0,1)
  Length = 0.6
  Length2 = 10
  Placement = pos=(0,0,0.2) rot=(0,0,1;0rad)
  Profile = -> Sketch087
  ReferenceAxis = -> Sketch087 [N_Axis]
  Refine = true
  Type = 0
FEATURE [PartDesign::Body] Body077  label="entretoises069"
  Group = -> [Sketch087,Pad074]
  Origin = -> Origin077
  Placement = pos=(504.546,-15.4212,0) rot=(0,0,-1;1.5708rad)
  Tip = -> Pad074
FEATURE [Sketcher::SketchObject] Sketch088
  FullyConstrained = true
  MapMode = 5
  Placement = pos=(0,0,0.2) rot=(0,0,1;0rad)
  sketch-geometry (1):
    g0: Circle CenterX=-4.75 CenterY=-214.65 CenterZ=0 NormalX=0 NormalY=0 NormalZ=1 AngleXU=0 Radius=1.05
  constraints (3):
    c: Diameter(g0) = 2.1
    c: Distance(g0,g-2) = 4.75
    c: Distance(g0,g-1) = 214.65
FEATURE [PartDesign::Pad] Pad075
  Direction = (0,0,1)
  Length = 0.6
  Length2 = 10
  Placement = pos=(0,0,0.2) rot=(0,0,1;0rad)
  Profile = -> Sketch088
  ReferenceAxis = -> Sketch088 [N_Axis]
  Refine = true
  Type = 0
FEATURE [PartDesign::Body] Body078  label="entretoises070"
  Group = -> [Sketch088,Pad075]
  Origin = -> Origin078
  Placement = pos=(504.546,-15.4212,0) rot=(0,0,-1;1.5708rad)
  Tip = -> Pad075
FEATURE [Sketcher::SketchObject] Sketch089
  FullyConstrained = true
  MapMode = 5
  Placement = pos=(0,0,0.2) rot=(0,0,1;0rad)
  sketch-geometry (1):
    g0: Circle CenterX=-4.75 CenterY=-224.75 CenterZ=0 NormalX=0 NormalY=0 NormalZ=1 AngleXU=0 Radius=1.05
  constraints (3):
    c: Diameter(g0) = 2.1
    c: Distance(g0,g-2) = 4.75
    c: Distance(g0,g-1) = 224.75
FEATURE [PartDesign::Pad] Pad076
  Direction = (0,0,1)
  Length = 0.6
  Length2 = 10
  Placement = pos=(0,0,0.2) rot=(0,0,1;0rad)
  Profile = -> Sketch089
  ReferenceAxis = -> Sketch089 [N_Axis]
  Refine = true
  Type = 0
FEATURE [PartDesign::Body] Body079  label="entretoises071"
  Group = -> [Sketch089,Pad076]
  Origin = -> Origin079
  Placement = pos=(504.546,-15.4212,0) rot=(0,0,-1;1.5708rad)
  Tip = -> Pad076
FEATURE [Sketcher::SketchObject] Sketch090
  FullyConstrained = true
  MapMode = 5
  Placement = pos=(0,0,0.2) rot=(0,0,1;0rad)
  sketch-geometry (1):
    g0: Circle CenterX=-4.75 CenterY=-234.85 CenterZ=0 NormalX=0 NormalY=0 NormalZ=1 AngleXU=0 Radius=1.05
  constraints (3):
    c: Diameter(g0) = 2.1
    c: Distance(g0,g-2) = 4.75
    c: Distance(g0,g-1) = 234.85
FEATURE [PartDesign::Pad] Pad077
  Direction = (0,0,1)
  Length = 0.6
  Length2 = 10
  Placement = pos=(0,0,0.2) rot=(0,0,1;0rad)
  Profile = -> Sketch090
  ReferenceAxis = -> Sketch090 [N_Axis]
  Refine = true
  Type = 0
FEATURE [PartDesign::Body] Body080  label="entretoises072"
  Group = -> [Sketch090,Pad077]
  Origin = -> Origin080
  Placement = pos=(504.546,-15.4212,0) rot=(0,0,-1;1.5708rad)
  Tip = -> Pad077
FEATURE [Sketcher::SketchObject] Sketch091
  FullyConstrained = true
  MapMode = 5
  Placement = pos=(0,0,0.2) rot=(0,0,1;0rad)
  sketch-geometry (1):
    g0: Circle CenterX=-4.75 CenterY=-244.95 CenterZ=0 NormalX=0 NormalY=0 NormalZ=1 AngleXU=0 Radius=1.05
  constraints (3):
    c: Diameter(g0) = 2.1
    c: Distance(g0,g-2) = 4.75
    c: Distance(g0,g-1) = 244.95
FEATURE [PartDesign::Pad] Pad078
  Direction = (0,0,1)
  Length = 0.6
  Length2 = 10
  Placement = pos=(0,0,0.2) rot=(0,0,1;0rad)
  Profile = -> Sketch091
  ReferenceAxis = -> Sketch091 [N_Axis]
  Refine = true
  Type = 0
FEATURE [PartDesign::Body] Body081  label="entretoises073"
  Group = -> [Sketch091,Pad078]
  Origin = -> Origin081
  Placement = pos=(504.546,-15.4212,0) rot=(0,0,-1;1.5708rad)
  Tip = -> Pad078
FEATURE [Sketcher::SketchObject] Sketch092
  FullyConstrained = true
  MapMode = 5
  Placement = pos=(0,0,0.2) rot=(0,0,1;0rad)
  sketch-geometry (1):
    g0: Circle CenterX=-4.75 CenterY=-255.05 CenterZ=0 NormalX=0 NormalY=0 NormalZ=1 AngleXU=0 Radius=1.05
  constraints (3):
    c: Diameter(g0) = 2.1
    c: Distance(g0,g-2) = 4.75
    c: Distance(g0,g-1) = 255.05
FEATURE [PartDesign::Pad] Pad079
  Direction = (0,0,1)
  Length = 0.6
  Length2 = 10
  Placement = pos=(0,0,0.2) rot=(0,0,1;0rad)
  Profile = -> Sketch092
  ReferenceAxis = -> Sketch092 [N_Axis]
  Refine = true
  Type = 0
FEATURE [PartDesign::Body] Body082  label="entretoises074"
  Group = -> [Sketch092,Pad079]
  Origin = -> Origin082
  Placement = pos=(504.546,-15.4212,0) rot=(0,0,-1;1.5708rad)
  Tip = -> Pad079
FEATURE [Sketcher::SketchObject] Sketch093
  FullyConstrained = true
  MapMode = 5
  Placement = pos=(0,0,0.2) rot=(0,0,1;0rad)
  sketch-geometry (1):
    g0: Circle CenterX=-4.75 CenterY=-265.15 CenterZ=0 NormalX=0 NormalY=0 NormalZ=1 AngleXU=0 Radius=1.05
  constraints (3):
    c: Diameter(g0) = 2.1
    c: Distance(g0,g-2) = 4.75
    c: Distance(g0,g-1) = 265.15
FEATURE [PartDesign::Pad] Pad080
  Direction = (0,0,1)
  Length = 0.6
  Length2 = 10
  Placement = pos=(0,0,0.2) rot=(0,0,1;0rad)
  Profile = -> Sketch093
  ReferenceAxis = -> Sketch093 [N_Axis]
  Refine = true
  Type = 0
FEATURE [PartDesign::Body] Body083  label="entretoises075"
  Group = -> [Sketch093,Pad080]
  Origin = -> Origin083
  Placement = pos=(504.546,-15.4212,0) rot=(0,0,-1;1.5708rad)
  Tip = -> Pad080
FEATURE [Sketcher::SketchObject] Sketch094
  FullyConstrained = true
  MapMode = 5
  Placement = pos=(0,0,0.2) rot=(0,0,1;0rad)
  sketch-geometry (1):
    g0: Circle CenterX=-4.75 CenterY=-275.25 CenterZ=0 NormalX=0 NormalY=0 NormalZ=1 AngleXU=0 Radius=1.05
  constraints (3):
    c: Diameter(g0) = 2.1
    c: Distance(g0,g-2) = 4.75
    c: Distance(g0,g-1) = 275.25
FEATURE [PartDesign::Pad] Pad081
  Direction = (0,0,1)
  Length = 0.6
  Length2 = 10
  Placement = pos=(0,0,0.2) rot=(0,0,1;0rad)
  Profile = -> Sketch094
  ReferenceAxis = -> Sketch094 [N_Axis]
  Refine = true
  Type = 0
FEATURE [PartDesign::Body] Body084  label="entretoises076"
  Group = -> [Sketch094,Pad081]
  Origin = -> Origin084
  Placement = pos=(504.546,-15.4212,0) rot=(0,0,-1;1.5708rad)
  Tip = -> Pad081
FEATURE [Sketcher::SketchObject] Sketch095
  FullyConstrained = true
  MapMode = 5
  Placement = pos=(0,0,0.2) rot=(0,0,1;0rad)
  sketch-geometry (1):
    g0: Circle CenterX=-4.75 CenterY=-285.35 CenterZ=0 NormalX=0 NormalY=0 NormalZ=1 AngleXU=0 Radius=1.05
  constraints (3):
    c: Diameter(g0) = 2.1
    c: Distance(g0,g-2) = 4.75
    c: Distance(g0,g-1) = 285.35
FEATURE [PartDesign::Pad] Pad082
  Direction = (0,0,1)
  Length = 0.6
  Length2 = 10
  Placement = pos=(0,0,0.2) rot=(0,0,1;0rad)
  Profile = -> Sketch095
  ReferenceAxis = -> Sketch095 [N_Axis]
  Refine = true
  Type = 0
FEATURE [PartDesign::Body] Body085  label="entretoises077"
  Group = -> [Sketch095,Pad082]
  Origin = -> Origin085
  Placement = pos=(504.546,-15.4212,0) rot=(0,0,-1;1.5708rad)
  Tip = -> Pad082
FEATURE [Sketcher::SketchObject] Sketch096
  FullyConstrained = true
  MapMode = 5
  Placement = pos=(0,0,0.2) rot=(0,0,1;0rad)
  sketch-geometry (1):
    g0: Circle CenterX=-4.75 CenterY=-295.45 CenterZ=0 NormalX=0 NormalY=0 NormalZ=1 AngleXU=0 Radius=1.05
  constraints (3):
    c: Diameter(g0) = 2.1
    c: Distance(g0,g-2) = 4.75
    c: Distance(g0,g-1) = 295.45
FEATURE [PartDesign::Pad] Pad083
  Direction = (0,0,1)
  Length = 0.6
  Length2 = 10
  Placement = pos=(0,0,0.2) rot=(0,0,1;0rad)
  Profile = -> Sketch096
  ReferenceAxis = -> Sketch096 [N_Axis]
  Refine = true
  Type = 0
FEATURE [PartDesign::Body] Body086  label="entretoises078"
  Group = -> [Sketch096,Pad083]
  Origin = -> Origin086
  Placement = pos=(504.546,-15.4212,0) rot=(0,0,-1;1.5708rad)
  Tip = -> Pad083
FEATURE [Sketcher::SketchObject] Sketch097
  FullyConstrained = true
  MapMode = 5
  Placement = pos=(0,0,0.2) rot=(0,0,1;0rad)
  sketch-geometry (1):
    g0: Circle CenterX=-4.75 CenterY=-305.55 CenterZ=0 NormalX=0 NormalY=0 NormalZ=1 AngleXU=0 Radius=1.05
  constraints (3):
    c: Diameter(g0) = 2.1
    c: Distance(g0,g-2) = 4.75
    c: Distance(g0,g-1) = 305.55
FEATURE [PartDesign::Pad] Pad084
  Direction = (0,0,1)
  Length = 0.6
  Length2 = 10
  Placement = pos=(0,0,0.2) rot=(0,0,1;0rad)
  Profile = -> Sketch097
  ReferenceAxis = -> Sketch097 [N_Axis]
  Refine = true
  Type = 0
FEATURE [PartDesign::Body] Body087  label="entretoises079"
  Group = -> [Sketch097,Pad084]
  Origin = -> Origin087
  Placement = pos=(504.546,-15.4212,0) rot=(0,0,-1;1.5708rad)
  Tip = -> Pad084
FEATURE [Sketcher::SketchObject] Sketch098
  FullyConstrained = true
  MapMode = 5
  Placement = pos=(0,0,0.2) rot=(0,0,1;0rad)
  sketch-geometry (1):
    g0: Circle CenterX=-4.75 CenterY=-315.65 CenterZ=0 NormalX=0 NormalY=0 NormalZ=1 AngleXU=0 Radius=1.05
  constraints (3):
    c: Diameter(g0) = 2.1
    c: Distance(g0,g-2) = 4.75
    c: Distance(g0,g-1) = 315.65
FEATURE [PartDesign::Pad] Pad085
  Direction = (0,0,1)
  Length = 0.6
  Length2 = 10
  Placement = pos=(0,0,0.2) rot=(0,0,1;0rad)
  Profile = -> Sketch098
  ReferenceAxis = -> Sketch098 [N_Axis]
  Refine = true
  Type = 0
FEATURE [PartDesign::Body] Body088  label="entretoises080"
  Group = -> [Sketch098,Pad085]
  Origin = -> Origin088
  Placement = pos=(504.546,-15.4212,0) rot=(0,0,-1;1.5708rad)
  Tip = -> Pad085
FEATURE [Sketcher::SketchObject] Sketch099
  FullyConstrained = true
  MapMode = 5
  Placement = pos=(0,0,0.2) rot=(0,0,1;0rad)
  sketch-geometry (1):
    g0: Circle CenterX=-4.75 CenterY=-325.75 CenterZ=0 NormalX=0 NormalY=0 NormalZ=1 AngleXU=0 Radius=1.05
  constraints (3):
    c: Diameter(g0) = 2.1
    c: Distance(g0,g-2) = 4.75
    c: Distance(g0,g-1) = 325.75
FEATURE [PartDesign::Pad] Pad086
  Direction = (0,0,1)
  Length = 0.6
  Length2 = 10
  Placement = pos=(0,0,0.2) rot=(0,0,1;0rad)
  Profile = -> Sketch099
  ReferenceAxis = -> Sketch099 [N_Axis]
  Refine = true
  Type = 0
FEATURE [PartDesign::Body] Body089  label="entretoises081"
  Group = -> [Sketch099,Pad086]
  Origin = -> Origin089
  Placement = pos=(504.546,-15.4212,0) rot=(0,0,-1;1.5708rad)
  Tip = -> Pad086
FEATURE [Sketcher::SketchObject] Sketch100
  FullyConstrained = true
  MapMode = 5
  Placement = pos=(0,0,0.2) rot=(0,0,1;0rad)
  sketch-geometry (1):
    g0: Circle CenterX=-4.75 CenterY=-335.85 CenterZ=0 NormalX=0 NormalY=0 NormalZ=1 AngleXU=0 Radius=1.05
  constraints (3):
    c: Diameter(g0) = 2.1
    c: Distance(g0,g-2) = 4.75
    c: Distance(g0,g-1) = 335.85
FEATURE [PartDesign::Pad] Pad087
  Direction = (0,0,1)
  Length = 0.6
  Length2 = 10
  Placement = pos=(0,0,0.2) rot=(0,0,1;0rad)
  Profile = -> Sketch100
  ReferenceAxis = -> Sketch100 [N_Axis]
  Refine = true
  Type = 0
FEATURE [PartDesign::Body] Body090  label="entretoises082"
  Group = -> [Sketch100,Pad087]
  Origin = -> Origin090
  Placement = pos=(504.546,-15.4212,0) rot=(0,0,-1;1.5708rad)
  Tip = -> Pad087
FEATURE [Sketcher::SketchObject] Sketch101
  FullyConstrained = true
  MapMode = 5
  Placement = pos=(0,0,0.2) rot=(0,0,1;0rad)
  sketch-geometry (1):
    g0: Circle CenterX=-4.75 CenterY=-345.95 CenterZ=0 NormalX=0 NormalY=0 NormalZ=1 AngleXU=0 Radius=1.05
  constraints (3):
    c: Diameter(g0) = 2.1
    c: Distance(g0,g-2) = 4.75
    c: Distance(g0,g-1) = 345.95
FEATURE [PartDesign::Pad] Pad088
  Direction = (0,0,1)
  Length = 0.6
  Length2 = 10
  Placement = pos=(0,0,0.2) rot=(0,0,1;0rad)
  Profile = -> Sketch101
  ReferenceAxis = -> Sketch101 [N_Axis]
  Refine = true
  Type = 0
FEATURE [PartDesign::Body] Body091  label="entretoises083"
  Group = -> [Sketch101,Pad088]
  Origin = -> Origin091
  Placement = pos=(504.546,-15.4212,0) rot=(0,0,-1;1.5708rad)
  Tip = -> Pad088
FEATURE [Sketcher::SketchObject] Sketch102
  FullyConstrained = true
  MapMode = 5
  Placement = pos=(0,0,0.2) rot=(0,0,1;0rad)
  sketch-geometry (1):
    g0: Circle CenterX=-4.75 CenterY=-356.05 CenterZ=0 NormalX=0 NormalY=0 NormalZ=1 AngleXU=0 Radius=1.05
  constraints (3):
    c: Diameter(g0) = 2.1
    c: Distance(g0,g-2) = 4.75
    c: Distance(g0,g-1) = 356.05
FEATURE [PartDesign::Pad] Pad089
  Direction = (0,0,1)
  Length = 0.6
  Length2 = 10
  Placement = pos=(0,0,0.2) rot=(0,0,1;0rad)
  Profile = -> Sketch102
  ReferenceAxis = -> Sketch102 [N_Axis]
  Refine = true
  Type = 0
FEATURE [PartDesign::Body] Body092  label="entretoises084"
  Group = -> [Sketch102,Pad089]
  Origin = -> Origin092
  Placement = pos=(504.546,-15.4212,0) rot=(0,0,-1;1.5708rad)
  Tip = -> Pad089
FEATURE [Sketcher::SketchObject] Sketch103
  FullyConstrained = true
  MapMode = 5
  Placement = pos=(0,0,0.2) rot=(0,0,1;0rad)
  sketch-geometry (1):
    g0: Circle CenterX=-4.75 CenterY=-366.15 CenterZ=0 NormalX=0 NormalY=0 NormalZ=1 AngleXU=0 Radius=1.05
  constraints (3):
    c: Diameter(g0) = 2.1
    c: Distance(g0,g-2) = 4.75
    c: Distance(g0,g-1) = 366.15
FEATURE [PartDesign::Pad] Pad090
  Direction = (0,0,1)
  Length = 0.6
  Length2 = 10
  Placement = pos=(0,0,0.2) rot=(0,0,1;0rad)
  Profile = -> Sketch103
  ReferenceAxis = -> Sketch103 [N_Axis]
  Refine = true
  Type = 0
FEATURE [PartDesign::Body] Body093  label="entretoises085"
  Group = -> [Sketch103,Pad090]
  Origin = -> Origin093
  Placement = pos=(504.546,-15.4212,0) rot=(0,0,-1;1.5708rad)
  Tip = -> Pad090
FEATURE [Sketcher::SketchObject] Sketch104
  FullyConstrained = true
  MapMode = 5
  Placement = pos=(0,0,0.2) rot=(0,0,1;0rad)
  sketch-geometry (1):
    g0: Circle CenterX=-4.75 CenterY=-376.25 CenterZ=0 NormalX=0 NormalY=0 NormalZ=1 AngleXU=0 Radius=1.05
  constraints (3):
    c: Diameter(g0) = 2.1
    c: Distance(g0,g-2) = 4.75
    c: Distance(g0,g-1) = 376.25
FEATURE [PartDesign::Pad] Pad091
  Direction = (0,0,1)
  Length = 0.6
  Length2 = 10
  Placement = pos=(0,0,0.2) rot=(0,0,1;0rad)
  Profile = -> Sketch104
  ReferenceAxis = -> Sketch104 [N_Axis]
  Refine = true
  Type = 0
FEATURE [PartDesign::Body] Body094  label="entretoises086"
  Group = -> [Sketch104,Pad091]
  Origin = -> Origin094
  Placement = pos=(504.546,-15.4212,0) rot=(0,0,-1;1.5708rad)
  Tip = -> Pad091
FEATURE [Sketcher::SketchObject] Sketch105
  FullyConstrained = true
  MapMode = 5
  Placement = pos=(0,0,0.2) rot=(0,0,1;0rad)
  sketch-geometry (1):
    g0: Circle CenterX=-4.75 CenterY=-386.35 CenterZ=0 NormalX=0 NormalY=0 NormalZ=1 AngleXU=0 Radius=1.05
  constraints (3):
    c: Diameter(g0) = 2.1
    c: Distance(g0,g-2) = 4.75
    c: Distance(g0,g-1) = 386.35
FEATURE [PartDesign::Pad] Pad092
  Direction = (0,0,1)
  Length = 0.6
  Length2 = 10
  Placement = pos=(0,0,0.2) rot=(0,0,1;0rad)
  Profile = -> Sketch105
  ReferenceAxis = -> Sketch105 [N_Axis]
  Refine = true
  Type = 0
FEATURE [PartDesign::Body] Body095  label="entretoises087"
  Group = -> [Sketch105,Pad092]
  Origin = -> Origin095
  Placement = pos=(504.546,-15.4212,0) rot=(0,0,-1;1.5708rad)
  Tip = -> Pad092
FEATURE [Sketcher::SketchObject] Sketch106
  FullyConstrained = true
  MapMode = 5
  Placement = pos=(0,0,0.2) rot=(0,0,1;0rad)
  sketch-geometry (1):
    g0: Circle CenterX=-4.75 CenterY=-396.45 CenterZ=0 NormalX=0 NormalY=0 NormalZ=1 AngleXU=0 Radius=1.05
  constraints (3):
    c: Diameter(g0) = 2.1
    c: Distance(g0,g-2) = 4.75
    c: Distance(g0,g-1) = 396.45
FEATURE [PartDesign::Pad] Pad093
  Direction = (0,0,1)
  Length = 0.6
  Length2 = 10
  Placement = pos=(0,0,0.2) rot=(0,0,1;0rad)
  Profile = -> Sketch106
  ReferenceAxis = -> Sketch106 [N_Axis]
  Refine = true
  Type = 0
FEATURE [PartDesign::Body] Body096  label="entretoises088"
  Group = -> [Sketch106,Pad093]
  Origin = -> Origin096
  Placement = pos=(504.546,-15.4212,0) rot=(0,0,-1;1.5708rad)
  Tip = -> Pad093
FEATURE [Sketcher::SketchObject] Sketch107
  FullyConstrained = true
  MapMode = 5
  Placement = pos=(0,0,0.2) rot=(0,0,1;0rad)
  sketch-geometry (1):
    g0: Circle CenterX=-4.75 CenterY=-406.55 CenterZ=0 NormalX=0 NormalY=0 NormalZ=1 AngleXU=0 Radius=1.05
  constraints (3):
    c: Diameter(g0) = 2.1
    c: Distance(g0,g-2) = 4.75
    c: Distance(g0,g-1) = 406.55
FEATURE [PartDesign::Pad] Pad094
  Direction = (0,0,1)
  Length = 0.6
  Length2 = 10
  Placement = pos=(0,0,0.2) rot=(0,0,1;0rad)
  Profile = -> Sketch107
  ReferenceAxis = -> Sketch107 [N_Axis]
  Refine = true
  Type = 0
FEATURE [PartDesign::Body] Body097  label="entretoises089"
  Group = -> [Sketch107,Pad094]
  Origin = -> Origin097
  Placement = pos=(504.546,-15.4212,0) rot=(0,0,-1;1.5708rad)
  Tip = -> Pad094
FEATURE [Sketcher::SketchObject] Sketch108
  FullyConstrained = true
  MapMode = 5
  Placement = pos=(0,0,0.2) rot=(0,0,1;0rad)
  sketch-geometry (1):
    g0: Circle CenterX=-4.75 CenterY=-416.65 CenterZ=0 NormalX=0 NormalY=0 NormalZ=1 AngleXU=0 Radius=1.05
  constraints (3):
    c: Diameter(g0) = 2.1
    c: Distance(g0,g-2) = 4.75
    c: Distance(g0,g-1) = 416.65
FEATURE [PartDesign::Pad] Pad095
  Direction = (0,0,1)
  Length = 0.6
  Length2 = 10
  Placement = pos=(0,0,0.2) rot=(0,0,1;0rad)
  Profile = -> Sketch108
  ReferenceAxis = -> Sketch108 [N_Axis]
  Refine = true
  Type = 0
FEATURE [PartDesign::Body] Body098  label="entretoises090"
  Group = -> [Sketch108,Pad095]
  Origin = -> Origin098
  Placement = pos=(504.546,-15.4212,0) rot=(0,0,-1;1.5708rad)
  Tip = -> Pad095
FEATURE [Sketcher::SketchObject] Sketch109
  FullyConstrained = true
  MapMode = 5
  Placement = pos=(0,0,0.2) rot=(0,0,1;0rad)
  sketch-geometry (1):
    g0: Circle CenterX=-4.75 CenterY=-426.75 CenterZ=0 NormalX=0 NormalY=0 NormalZ=1 AngleXU=0 Radius=1.05
  constraints (3):
    c: Diameter(g0) = 2.1
    c: Distance(g0,g-2) = 4.75
    c: Distance(g0,g-1) = 426.75
FEATURE [PartDesign::Pad] Pad096
  Direction = (0,0,1)
  Length = 0.6
  Length2 = 10
  Placement = pos=(0,0,0.2) rot=(0,0,1;0rad)
  Profile = -> Sketch109
  ReferenceAxis = -> Sketch109 [N_Axis]
  Refine = true
  Type = 0
FEATURE [PartDesign::Body] Body099  label="entretoises091"
  Group = -> [Sketch109,Pad096]
  Origin = -> Origin099
  Placement = pos=(504.546,-15.4212,0) rot=(0,0,-1;1.5708rad)
  Tip = -> Pad096
FEATURE [Sketcher::SketchObject] Sketch110
  FullyConstrained = true
  MapMode = 5
  Placement = pos=(0,0,0.2) rot=(0,0,1;0rad)
  sketch-geometry (1):
    g0: Circle CenterX=-4.75 CenterY=-436.85 CenterZ=0 NormalX=0 NormalY=0 NormalZ=1 AngleXU=0 Radius=1.05
  constraints (3):
    c: Diameter(g0) = 2.1
    c: Distance(g0,g-2) = 4.75
    c: Distance(g0,g-1) = 436.85
FEATURE [PartDesign::Pad] Pad097
  Direction = (0,0,1)
  Length = 0.6
  Length2 = 10
  Placement = pos=(0,0,0.2) rot=(0,0,1;0rad)
  Profile = -> Sketch110
  ReferenceAxis = -> Sketch110 [N_Axis]
  Refine = true
  Type = 0
FEATURE [PartDesign::Body] Body100  label="entretoises092"
  Group = -> [Sketch110,Pad097]
  Origin = -> Origin100
  Placement = pos=(504.546,-15.4212,0) rot=(0,0,-1;1.5708rad)
  Tip = -> Pad097
FEATURE [Sketcher::SketchObject] Sketch111
  FullyConstrained = true
  MapMode = 5
  Placement = pos=(0,0,0.2) rot=(0,0,1;0rad)
  sketch-geometry (1):
    g0: Circle CenterX=-4.75 CenterY=-457.05 CenterZ=0 NormalX=0 NormalY=0 NormalZ=1 AngleXU=0 Radius=1.05
  constraints (3):
    c: Diameter(g0) = 2.1
    c: Distance(g0,g-2) = 4.75
    c: Distance(g0,g-1) = 457.05
FEATURE [PartDesign::Pad] Pad098
  Direction = (0,0,1)
  Length = 0.6
  Length2 = 10
  Placement = pos=(0,0,0.2) rot=(0,0,1;0rad)
  Profile = -> Sketch111
  ReferenceAxis = -> Sketch111 [N_Axis]
  Refine = true
  Type = 0
FEATURE [PartDesign::Body] Body101  label="entretoises093"
  Group = -> [Sketch111,Pad098]
  Origin = -> Origin101
  Placement = pos=(504.546,-15.4212,0) rot=(0,0,-1;1.5708rad)
  Tip = -> Pad098
FEATURE [Sketcher::SketchObject] Sketch112
  FullyConstrained = true
  MapMode = 5
  Placement = pos=(0,0,0.2) rot=(0,0,1;0rad)
  sketch-geometry (1):
    g0: Circle CenterX=-4.75 CenterY=-467.15 CenterZ=0 NormalX=0 NormalY=0 NormalZ=1 AngleXU=0 Radius=1.05
  constraints (3):
    c: Diameter(g0) = 2.1
    c: Distance(g0,g-2) = 4.75
    c: Distance(g0,g-1) = 467.15
FEATURE [PartDesign::Pad] Pad099
  Direction = (0,0,1)
  Length = 0.6
  Length2 = 10
  Placement = pos=(0,0,0.2) rot=(0,0,1;0rad)
  Profile = -> Sketch112
  ReferenceAxis = -> Sketch112 [N_Axis]
  Refine = true
  Type = 0
FEATURE [PartDesign::Body] Body102  label="entretoises094"
  Group = -> [Sketch112,Pad099]
  Origin = -> Origin102
  Placement = pos=(504.546,-15.4212,0) rot=(0,0,-1;1.5708rad)
  Tip = -> Pad099
FEATURE [Sketcher::SketchObject] Sketch113
  FullyConstrained = true
  MapMode = 5
  Placement = pos=(0,0,0.2) rot=(0,0,1;0rad)
  sketch-geometry (1):
    g0: Circle CenterX=-4.75 CenterY=-477.25 CenterZ=0 NormalX=0 NormalY=0 NormalZ=1 AngleXU=0 Radius=1.05
  constraints (3):
    c: Diameter(g0) = 2.1
    c: Distance(g0,g-2) = 4.75
    c: Distance(g0,g-1) = 477.25
FEATURE [PartDesign::Pad] Pad100
  Direction = (0,0,1)
  Length = 0.6
  Length2 = 10
  Placement = pos=(0,0,0.2) rot=(0,0,1;0rad)
  Profile = -> Sketch113
  ReferenceAxis = -> Sketch113 [N_Axis]
  Refine = true
  Type = 0
FEATURE [PartDesign::Body] Body103  label="entretoises095"
  Group = -> [Sketch113,Pad100]
  Origin = -> Origin103
  Placement = pos=(504.546,-15.4212,0) rot=(0,0,-1;1.5708rad)
  Tip = -> Pad100
FEATURE [Sketcher::SketchObject] Sketch114
  FullyConstrained = true
  MapMode = 5
  Placement = pos=(0,0,0.2) rot=(0,0,1;0rad)
  sketch-geometry (1):
    g0: Circle CenterX=-4.75 CenterY=-487.35 CenterZ=0 NormalX=0 NormalY=0 NormalZ=1 AngleXU=0 Radius=1.05
  constraints (3):
    c: Diameter(g0) = 2.1
    c: Distance(g0,g-2) = 4.75
    c: Distance(g0,g-1) = 487.35
FEATURE [PartDesign::Pad] Pad101
  Direction = (0,0,1)
  Length = 0.6
  Length2 = 10
  Placement = pos=(0,0,0.2) rot=(0,0,1;0rad)
  Profile = -> Sketch114
  ReferenceAxis = -> Sketch114 [N_Axis]
  Refine = true
  Type = 0
FEATURE [PartDesign::Body] Body104  label="entretoises096"
  Group = -> [Sketch114,Pad101]
  Origin = -> Origin104
  Placement = pos=(504.546,-15.4212,0) rot=(0,0,-1;1.5708rad)
  Tip = -> Pad101
FEATURE [Sketcher::SketchObject] Sketch115
  FullyConstrained = true
  MapMode = 5
  Placement = pos=(0,0,0.2) rot=(0,0,1;0rad)
  sketch-geometry (1):
    g0: Circle CenterX=-4.75 CenterY=-446.95 CenterZ=0 NormalX=0 NormalY=0 NormalZ=1 AngleXU=0 Radius=1.05
  constraints (3):
    c: Diameter(g0) = 2.1
    c: Distance(g0,g-2) = 4.75
    c: Distance(g0,g-1) = 446.95
FEATURE [PartDesign::Pad] Pad102
  Direction = (0,0,1)
  Length = 0.6
  Length2 = 10
  Placement = pos=(0,0,0.2) rot=(0,0,1;0rad)
  Profile = -> Sketch115
  ReferenceAxis = -> Sketch115 [N_Axis]
  Refine = true
  Type = 0
FEATURE [PartDesign::Body] Body105  label="entretoises097"
  Group = -> [Sketch115,Pad102]
  Origin = -> Origin105
  Placement = pos=(504.546,-15.4212,0) rot=(0,0,-1;1.5708rad)
  Tip = -> Pad102
FEATURE [App::DocumentObjectGroup] Group002  label="cadre arriere"
  Group = -> [Body105,Body104,Body103,Body093,Body094,Body095,Body096,Body097,Body098,Body099,Body100,Body101,Body102,Body079,Body080,Body081,Body082,Body083,Body084,Body085,Body086,Body087,Body088,Body089,Body090,Body091,Body092,Body068,Body069,Body070,Body071,Body072,Body073,Body074,Body075,Body076,Body077,Body078,Body059,Body060,Body061,Body062,Body063,Body064,Body065,Body066,Body067,Body053,Body054,Body055,+3 more]
FEATURE [Fem::ConstraintFixed] ConstraintFixed
  NormalDirection = (-1,0,0)
  Normals = (8) [(-1,0,0),(-1,0,0),(-1,0,0),(-1,0,0),(-1,0,0),(-1,0,0),(-1,0,0),(-1,0,0)]
  Points = (8) [(0,-500,9.5),(0,-333.333,-1.72883e-14),(0,-333.333,4.75),(0,-333.333,9.5),(0,-166.667,-3.56217e-14),(0,-166.667,4.75),(0,-166.667,9.5),(0,1.045e-15,9.5)]
  References = -> [Pocket005]
FEATURE [Fem::ConstraintForce] ConstraintForce
  Direction = -> Pocket005 [Edge7]
  DirectionVector = (1,0,0)
  Force = 0
  NormalDirection = (1,0,0)
  Points = (8) [(1,-500,9.5),(1,-333.333,9.5),(1,-333.333,4.75),(1,-333.333,3.73035e-14),(1,-166.667,9.5),(1,-166.667,4.75),(1,-166.667,1.77636e-14),(1,1.05e-15,9.5)]
  References = -> [Pocket005]
FEATURE [App::MaterialObjectPython] MaterialSolid  # material (typed FeaturePython)
  Category = 0
  Material = AmbientColor=(0.0020, 0.0020, 0.0020, 1.0); Author=M. Münch; AuthorAndLicense=LGPL-2.0-or-later; CardName=Steel-X5CrNi18-10; Density=7.8e-06 kg/mm^3; DiffuseColor=(0.0000, 0.0000, 0.0000, 1.0); EmissiveColor=(0.0000, 0.0000, 0.0000, 1.0); Father=Metal; KindOfMaterial=Stainless steel; License=LGPL-2.0-or-later; MaterialNumber=1.4301; Name=Steel-X5CrNi18-10; PoissonRatio=0.3; ShearModulus=8.1e+07 kg/(mm*s^2); Shininess=0.06; SpecularColor=(0.9800, 0.9800, 0.9800, 1.0); StandardCode=EN 10088; ThermalExpansionCoefficient=1.1e-05 1/K; Transparency=0; UltimateStrain=40; UltimateTensileStrength=520000 kg/(mm*s^2); YieldStrength=210000 kg/(mm*s^2); YoungsModulus=2e+08 kg/(mm*s^2)
  UUID = e5329208-0c38-47ec-8c59-e7bf6a35801d
FEATURE [Fem::FemAnalysis] Analysis
  Group = -> [ConstraintFixed,ConstraintForce,MaterialSolid]
